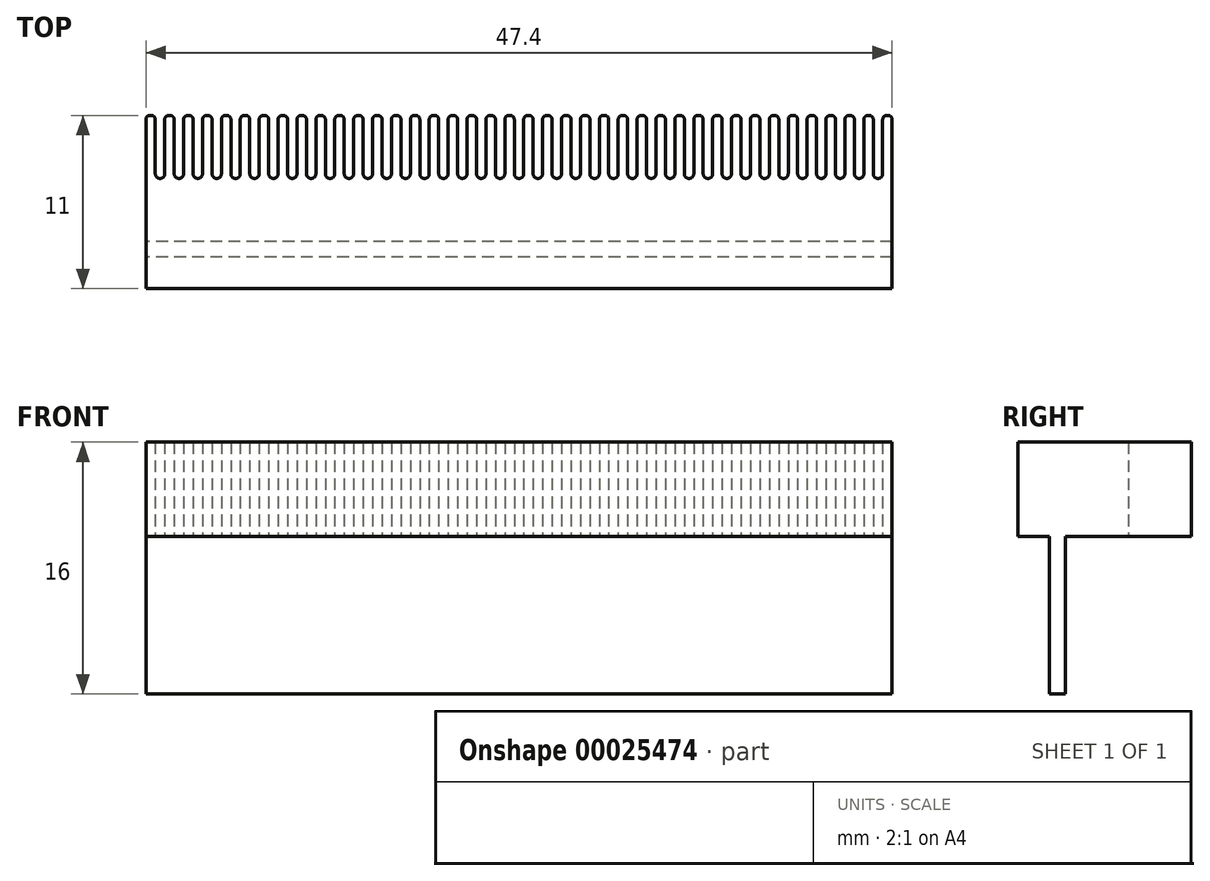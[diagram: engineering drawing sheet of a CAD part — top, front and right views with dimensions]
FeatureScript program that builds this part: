
annotation { "Feature Type Name" : "Feature", "Feature Type Description" : "" }
export const myFeature = defineFeature(function(context is Context, id is Id, definition is map)
    precondition{}
    {
        {
            var Q0;
            Q0=qCreatedBy(makeId("Top.planeOp"),FACE);
            var sketch = newSketch(context, id + "F0", { "sketchPlane" : qUnion([Q0])});
            skLineSegment(sketch, "E0", {"start": v(-0.6, 7) * mm, "end": v(-0.6, 7) * mm});
            skLineSegment(sketch, "E1", {"start": v(-0.3, 7.3) * mm, "end": v(-0.3, 10.75) * mm});
            skLineSegment(sketch, "E2", {"start": v(-0.05, 11) * mm, "end": v(0.05, 11) * mm});
            skLineSegment(sketch, "E3", {"start": v(0.3, 10.75) * mm, "end": v(0.3, 7.3) * mm});
            skLineSegment(sketch, "E4", {"start": v(0.6, 7) * mm, "end": v(0.6, 7) * mm});
            skLineSegment(sketch, "E5", {"start": v(0.6, 7) * mm, "end": v(0.6, 0) * mm});
            skLineSegment(sketch, "E6", {"start": v(0.6, 0) * mm, "end": v(-0.6, 0) * mm});
            skLineSegment(sketch, "E7", {"start": v(-0.6, 0) * mm, "end": v(-0.6, 7) * mm});
            skLineSegment(sketch, "E8.direction1", {"start": v(-7.3, 0) * mm, "end": v(-0.6, 0) * mm, "construction": true});
            skPoint(sketch, "E9.visualSharp", {"position": v(-0.3, 11) * mm});
            skArc(sketch, "E9.filletArc", {"start": v(-0.05, 11) * mm, "mid": v(-0.23, 10.93) * mm, "end": v(-0.3, 10.75) * mm});
            skPoint(sketch, "E10.visualSharp", {"position": v(0.3, 11) * mm});
            skArc(sketch, "E10.filletArc", {"start": v(0.3, 10.75) * mm, "mid": v(0.23, 10.93) * mm, "end": v(0.05, 11) * mm});
            skPoint(sketch, "E11.visualSharp", {"position": v(0.3, 7) * mm});
            skArc(sketch, "E11.filletArc", {"start": v(0.3, 7.3) * mm, "mid": v(0.39, 7.09) * mm, "end": v(0.6, 7) * mm});
            skPoint(sketch, "E12.visualSharp", {"position": v(-0.3, 7) * mm});
            skArc(sketch, "E12.filletArc", {"start": v(-0.6, 7) * mm, "mid": v(-0.39, 7.09) * mm, "end": v(-0.3, 7.3) * mm});
            skLineSegment(sketch, "E13.1.0.0", {"start": v(1.8, 0) * mm, "end": v(0.6, 0) * mm});
            skPoint(sketch, "E13.1.0.1", {"position": v(1.5, 7) * mm});
            skLineSegment(sketch, "E13.1.0.2", {"start": v(1.8, 7) * mm, "end": v(1.8, 0) * mm});
            skLineSegment(sketch, "E13.1.0.3", {"start": v(1.5, 10.75) * mm, "end": v(1.5, 7.3) * mm});
            skPoint(sketch, "E13.1.0.4", {"position": v(1.5, 11) * mm});
            skPoint(sketch, "E13.1.0.5", {"position": v(0.9, 7) * mm});
            skLineSegment(sketch, "E13.1.0.6", {"start": v(0.6, 0) * mm, "end": v(0.6, 7) * mm});
            skPoint(sketch, "E13.1.0.7", {"position": v(0.9, 11) * mm});
            skLineSegment(sketch, "E13.1.0.8", {"start": v(0.9, 7.3) * mm, "end": v(0.9, 10.75) * mm});
            skArc(sketch, "E13.1.0.9", {"start": v(1.5, 10.75) * mm, "mid": v(1.43, 10.93) * mm, "end": v(1.25, 11) * mm});
            skLineSegment(sketch, "E13.1.0.10", {"start": v(-6.1, 0) * mm, "end": v(0.6, 0) * mm, "construction": true});
            skArc(sketch, "E13.1.0.11", {"start": v(1.15, 11) * mm, "mid": v(0.97, 10.93) * mm, "end": v(0.9, 10.75) * mm});
            skArc(sketch, "E13.1.0.12", {"start": v(0.6, 7) * mm, "mid": v(0.81, 7.09) * mm, "end": v(0.9, 7.3) * mm});
            skArc(sketch, "E13.1.0.13", {"start": v(1.5, 7.3) * mm, "mid": v(1.59, 7.09) * mm, "end": v(1.8, 7) * mm});
            skLineSegment(sketch, "E13.1.0.14", {"start": v(1.15, 11) * mm, "end": v(1.25, 11) * mm});
            skLineSegment(sketch, "E13.2.0.0", {"start": v(3, 0) * mm, "end": v(1.8, 0) * mm});
            skPoint(sketch, "E13.2.0.1", {"position": v(2.7, 7) * mm});
            skLineSegment(sketch, "E13.2.0.2", {"start": v(3, 7) * mm, "end": v(3, 0) * mm});
            skLineSegment(sketch, "E13.2.0.3", {"start": v(2.7, 10.75) * mm, "end": v(2.7, 7.3) * mm});
            skPoint(sketch, "E13.2.0.4", {"position": v(2.7, 11) * mm});
            skPoint(sketch, "E13.2.0.5", {"position": v(2.1, 7) * mm});
            skLineSegment(sketch, "E13.2.0.6", {"start": v(1.8, 0) * mm, "end": v(1.8, 7) * mm});
            skPoint(sketch, "E13.2.0.7", {"position": v(2.1, 11) * mm});
            skLineSegment(sketch, "E13.2.0.8", {"start": v(2.1, 7.3) * mm, "end": v(2.1, 10.75) * mm});
            skArc(sketch, "E13.2.0.9", {"start": v(2.7, 10.75) * mm, "mid": v(2.63, 10.93) * mm, "end": v(2.45, 11) * mm});
            skLineSegment(sketch, "E13.2.0.10", {"start": v(-4.9, 0) * mm, "end": v(1.8, 0) * mm, "construction": true});
            skArc(sketch, "E13.2.0.11", {"start": v(2.35, 11) * mm, "mid": v(2.17, 10.93) * mm, "end": v(2.1, 10.75) * mm});
            skArc(sketch, "E13.2.0.12", {"start": v(1.8, 7) * mm, "mid": v(2.01, 7.09) * mm, "end": v(2.1, 7.3) * mm});
            skArc(sketch, "E13.2.0.13", {"start": v(2.7, 7.3) * mm, "mid": v(2.79, 7.09) * mm, "end": v(3, 7) * mm});
            skLineSegment(sketch, "E13.2.0.14", {"start": v(2.35, 11) * mm, "end": v(2.45, 11) * mm});
            skLineSegment(sketch, "E13.3.0.0", {"start": v(4.2, 0) * mm, "end": v(3, 0) * mm});
            skPoint(sketch, "E13.3.0.1", {"position": v(3.9, 7) * mm});
            skLineSegment(sketch, "E13.3.0.2", {"start": v(4.2, 7) * mm, "end": v(4.2, 0) * mm});
            skLineSegment(sketch, "E13.3.0.3", {"start": v(3.9, 10.75) * mm, "end": v(3.9, 7.3) * mm});
            skPoint(sketch, "E13.3.0.4", {"position": v(3.9, 11) * mm});
            skPoint(sketch, "E13.3.0.5", {"position": v(3.3, 7) * mm});
            skLineSegment(sketch, "E13.3.0.6", {"start": v(3, 0) * mm, "end": v(3, 7) * mm});
            skPoint(sketch, "E13.3.0.7", {"position": v(3.3, 11) * mm});
            skLineSegment(sketch, "E13.3.0.8", {"start": v(3.3, 7.3) * mm, "end": v(3.3, 10.75) * mm});
            skArc(sketch, "E13.3.0.9", {"start": v(3.9, 10.75) * mm, "mid": v(3.83, 10.93) * mm, "end": v(3.65, 11) * mm});
            skLineSegment(sketch, "E13.3.0.10", {"start": v(-3.7, 0) * mm, "end": v(3, 0) * mm, "construction": true});
            skArc(sketch, "E13.3.0.11", {"start": v(3.55, 11) * mm, "mid": v(3.37, 10.93) * mm, "end": v(3.3, 10.75) * mm});
            skArc(sketch, "E13.3.0.12", {"start": v(3, 7) * mm, "mid": v(3.21, 7.09) * mm, "end": v(3.3, 7.3) * mm});
            skArc(sketch, "E13.3.0.13", {"start": v(3.9, 7.3) * mm, "mid": v(3.99, 7.09) * mm, "end": v(4.2, 7) * mm});
            skLineSegment(sketch, "E13.3.0.14", {"start": v(3.55, 11) * mm, "end": v(3.65, 11) * mm});
            skLineSegment(sketch, "E13.4.0.0", {"start": v(5.4, 0) * mm, "end": v(4.2, 0) * mm});
            skPoint(sketch, "E13.4.0.1", {"position": v(5.1, 7) * mm});
            skLineSegment(sketch, "E13.4.0.2", {"start": v(5.4, 7) * mm, "end": v(5.4, 0) * mm});
            skLineSegment(sketch, "E13.4.0.3", {"start": v(5.1, 10.75) * mm, "end": v(5.1, 7.3) * mm});
            skPoint(sketch, "E13.4.0.4", {"position": v(5.1, 11) * mm});
            skPoint(sketch, "E13.4.0.5", {"position": v(4.5, 7) * mm});
            skLineSegment(sketch, "E13.4.0.6", {"start": v(4.2, 0) * mm, "end": v(4.2, 7) * mm});
            skPoint(sketch, "E13.4.0.7", {"position": v(4.5, 11) * mm});
            skLineSegment(sketch, "E13.4.0.8", {"start": v(4.5, 7.3) * mm, "end": v(4.5, 10.75) * mm});
            skArc(sketch, "E13.4.0.9", {"start": v(5.1, 10.75) * mm, "mid": v(5.03, 10.93) * mm, "end": v(4.85, 11) * mm});
            skLineSegment(sketch, "E13.4.0.10", {"start": v(-2.5, 0) * mm, "end": v(4.2, 0) * mm, "construction": true});
            skArc(sketch, "E13.4.0.11", {"start": v(4.75, 11) * mm, "mid": v(4.57, 10.93) * mm, "end": v(4.5, 10.75) * mm});
            skArc(sketch, "E13.4.0.12", {"start": v(4.2, 7) * mm, "mid": v(4.41, 7.09) * mm, "end": v(4.5, 7.3) * mm});
            skArc(sketch, "E13.4.0.13", {"start": v(5.1, 7.3) * mm, "mid": v(5.19, 7.09) * mm, "end": v(5.4, 7) * mm});
            skLineSegment(sketch, "E13.4.0.14", {"start": v(4.75, 11) * mm, "end": v(4.85, 11) * mm});
            skLineSegment(sketch, "E13.5.0.0", {"start": v(6.6, 0) * mm, "end": v(5.4, 0) * mm});
            skPoint(sketch, "E13.5.0.1", {"position": v(6.3, 7) * mm});
            skLineSegment(sketch, "E13.5.0.2", {"start": v(6.6, 7) * mm, "end": v(6.6, 0) * mm});
            skLineSegment(sketch, "E13.5.0.3", {"start": v(6.3, 10.75) * mm, "end": v(6.3, 7.3) * mm});
            skPoint(sketch, "E13.5.0.4", {"position": v(6.3, 11) * mm});
            skPoint(sketch, "E13.5.0.5", {"position": v(5.7, 7) * mm});
            skLineSegment(sketch, "E13.5.0.6", {"start": v(5.4, 0) * mm, "end": v(5.4, 7) * mm});
            skPoint(sketch, "E13.5.0.7", {"position": v(5.7, 11) * mm});
            skLineSegment(sketch, "E13.5.0.8", {"start": v(5.7, 7.3) * mm, "end": v(5.7, 10.75) * mm});
            skArc(sketch, "E13.5.0.9", {"start": v(6.3, 10.75) * mm, "mid": v(6.23, 10.93) * mm, "end": v(6.05, 11) * mm});
            skLineSegment(sketch, "E13.5.0.10", {"start": v(-1.3, 0) * mm, "end": v(5.4, 0) * mm, "construction": true});
            skArc(sketch, "E13.5.0.11", {"start": v(5.95, 11) * mm, "mid": v(5.77, 10.93) * mm, "end": v(5.7, 10.75) * mm});
            skArc(sketch, "E13.5.0.12", {"start": v(5.4, 7) * mm, "mid": v(5.61, 7.09) * mm, "end": v(5.7, 7.3) * mm});
            skArc(sketch, "E13.5.0.13", {"start": v(6.3, 7.3) * mm, "mid": v(6.39, 7.09) * mm, "end": v(6.6, 7) * mm});
            skLineSegment(sketch, "E13.5.0.14", {"start": v(5.95, 11) * mm, "end": v(6.05, 11) * mm});
            skLineSegment(sketch, "E13.6.0.0", {"start": v(7.8, 0) * mm, "end": v(6.6, 0) * mm});
            skPoint(sketch, "E13.6.0.1", {"position": v(7.5, 7) * mm});
            skLineSegment(sketch, "E13.6.0.2", {"start": v(7.8, 7) * mm, "end": v(7.8, 0) * mm});
            skLineSegment(sketch, "E13.6.0.3", {"start": v(7.5, 10.75) * mm, "end": v(7.5, 7.3) * mm});
            skPoint(sketch, "E13.6.0.4", {"position": v(7.5, 11) * mm});
            skPoint(sketch, "E13.6.0.5", {"position": v(6.9, 7) * mm});
            skLineSegment(sketch, "E13.6.0.6", {"start": v(6.6, 0) * mm, "end": v(6.6, 7) * mm});
            skPoint(sketch, "E13.6.0.7", {"position": v(6.9, 11) * mm});
            skLineSegment(sketch, "E13.6.0.8", {"start": v(6.9, 7.3) * mm, "end": v(6.9, 10.75) * mm});
            skArc(sketch, "E13.6.0.9", {"start": v(7.5, 10.75) * mm, "mid": v(7.43, 10.93) * mm, "end": v(7.25, 11) * mm});
            skLineSegment(sketch, "E13.6.0.10", {"start": v(-0.1, 0) * mm, "end": v(6.6, 0) * mm, "construction": true});
            skArc(sketch, "E13.6.0.11", {"start": v(7.15, 11) * mm, "mid": v(6.97, 10.93) * mm, "end": v(6.9, 10.75) * mm});
            skArc(sketch, "E13.6.0.12", {"start": v(6.6, 7) * mm, "mid": v(6.81, 7.09) * mm, "end": v(6.9, 7.3) * mm});
            skArc(sketch, "E13.6.0.13", {"start": v(7.5, 7.3) * mm, "mid": v(7.59, 7.09) * mm, "end": v(7.8, 7) * mm});
            skLineSegment(sketch, "E13.6.0.14", {"start": v(7.15, 11) * mm, "end": v(7.25, 11) * mm});
            skLineSegment(sketch, "E13.7.0.0", {"start": v(9, 0) * mm, "end": v(7.8, 0) * mm});
            skPoint(sketch, "E13.7.0.1", {"position": v(8.7, 7) * mm});
            skLineSegment(sketch, "E13.7.0.2", {"start": v(9, 7) * mm, "end": v(9, 0) * mm});
            skLineSegment(sketch, "E13.7.0.3", {"start": v(8.7, 10.75) * mm, "end": v(8.7, 7.3) * mm});
            skPoint(sketch, "E13.7.0.4", {"position": v(8.7, 11) * mm});
            skPoint(sketch, "E13.7.0.5", {"position": v(8.1, 7) * mm});
            skLineSegment(sketch, "E13.7.0.6", {"start": v(7.8, 0) * mm, "end": v(7.8, 7) * mm});
            skPoint(sketch, "E13.7.0.7", {"position": v(8.1, 11) * mm});
            skLineSegment(sketch, "E13.7.0.8", {"start": v(8.1, 7.3) * mm, "end": v(8.1, 10.75) * mm});
            skArc(sketch, "E13.7.0.9", {"start": v(8.7, 10.75) * mm, "mid": v(8.63, 10.93) * mm, "end": v(8.45, 11) * mm});
            skLineSegment(sketch, "E13.7.0.10", {"start": v(1.1, 0) * mm, "end": v(7.8, 0) * mm, "construction": true});
            skArc(sketch, "E13.7.0.11", {"start": v(8.35, 11) * mm, "mid": v(8.17, 10.93) * mm, "end": v(8.1, 10.75) * mm});
            skArc(sketch, "E13.7.0.12", {"start": v(7.8, 7) * mm, "mid": v(8.01, 7.09) * mm, "end": v(8.1, 7.3) * mm});
            skArc(sketch, "E13.7.0.13", {"start": v(8.7, 7.3) * mm, "mid": v(8.79, 7.09) * mm, "end": v(9, 7) * mm});
            skLineSegment(sketch, "E13.7.0.14", {"start": v(8.35, 11) * mm, "end": v(8.45, 11) * mm});
            skLineSegment(sketch, "E13.8.0.0", {"start": v(10.2, 0) * mm, "end": v(9, 0) * mm});
            skPoint(sketch, "E13.8.0.1", {"position": v(9.9, 7) * mm});
            skLineSegment(sketch, "E13.8.0.2", {"start": v(10.2, 7) * mm, "end": v(10.2, 0) * mm});
            skLineSegment(sketch, "E13.8.0.3", {"start": v(9.9, 10.75) * mm, "end": v(9.9, 7.3) * mm});
            skPoint(sketch, "E13.8.0.4", {"position": v(9.9, 11) * mm});
            skPoint(sketch, "E13.8.0.5", {"position": v(9.3, 7) * mm});
            skLineSegment(sketch, "E13.8.0.6", {"start": v(9, 0) * mm, "end": v(9, 7) * mm});
            skPoint(sketch, "E13.8.0.7", {"position": v(9.3, 11) * mm});
            skLineSegment(sketch, "E13.8.0.8", {"start": v(9.3, 7.3) * mm, "end": v(9.3, 10.75) * mm});
            skArc(sketch, "E13.8.0.9", {"start": v(9.9, 10.75) * mm, "mid": v(9.83, 10.93) * mm, "end": v(9.65, 11) * mm});
            skLineSegment(sketch, "E13.8.0.10", {"start": v(2.3, 0) * mm, "end": v(9, 0) * mm, "construction": true});
            skArc(sketch, "E13.8.0.11", {"start": v(9.55, 11) * mm, "mid": v(9.37, 10.93) * mm, "end": v(9.3, 10.75) * mm});
            skArc(sketch, "E13.8.0.12", {"start": v(9, 7) * mm, "mid": v(9.21, 7.09) * mm, "end": v(9.3, 7.3) * mm});
            skArc(sketch, "E13.8.0.13", {"start": v(9.9, 7.3) * mm, "mid": v(9.99, 7.09) * mm, "end": v(10.2, 7) * mm});
            skLineSegment(sketch, "E13.8.0.14", {"start": v(9.55, 11) * mm, "end": v(9.65, 11) * mm});
            skLineSegment(sketch, "E13.9.0.0", {"start": v(11.4, 0) * mm, "end": v(10.2, 0) * mm});
            skPoint(sketch, "E13.9.0.1", {"position": v(11.1, 7) * mm});
            skLineSegment(sketch, "E13.9.0.2", {"start": v(11.4, 7) * mm, "end": v(11.4, 0) * mm});
            skLineSegment(sketch, "E13.9.0.3", {"start": v(11.1, 10.75) * mm, "end": v(11.1, 7.3) * mm});
            skPoint(sketch, "E13.9.0.4", {"position": v(11.1, 11) * mm});
            skPoint(sketch, "E13.9.0.5", {"position": v(10.5, 7) * mm});
            skLineSegment(sketch, "E13.9.0.6", {"start": v(10.2, 0) * mm, "end": v(10.2, 7) * mm});
            skPoint(sketch, "E13.9.0.7", {"position": v(10.5, 11) * mm});
            skLineSegment(sketch, "E13.9.0.8", {"start": v(10.5, 7.3) * mm, "end": v(10.5, 10.75) * mm});
            skArc(sketch, "E13.9.0.9", {"start": v(11.1, 10.75) * mm, "mid": v(11.03, 10.93) * mm, "end": v(10.85, 11) * mm});
            skLineSegment(sketch, "E13.9.0.10", {"start": v(3.5, 0) * mm, "end": v(10.2, 0) * mm, "construction": true});
            skArc(sketch, "E13.9.0.11", {"start": v(10.75, 11) * mm, "mid": v(10.57, 10.93) * mm, "end": v(10.5, 10.75) * mm});
            skArc(sketch, "E13.9.0.12", {"start": v(10.2, 7) * mm, "mid": v(10.41, 7.09) * mm, "end": v(10.5, 7.3) * mm});
            skArc(sketch, "E13.9.0.13", {"start": v(11.1, 7.3) * mm, "mid": v(11.19, 7.09) * mm, "end": v(11.4, 7) * mm});
            skLineSegment(sketch, "E13.9.0.14", {"start": v(10.75, 11) * mm, "end": v(10.85, 11) * mm});
            skLineSegment(sketch, "E13.10.0.0", {"start": v(12.6, 0) * mm, "end": v(11.4, 0) * mm});
            skPoint(sketch, "E13.10.0.1", {"position": v(12.3, 7) * mm});
            skLineSegment(sketch, "E13.10.0.2", {"start": v(12.6, 7) * mm, "end": v(12.6, 0) * mm});
            skLineSegment(sketch, "E13.10.0.3", {"start": v(12.3, 10.75) * mm, "end": v(12.3, 7.3) * mm});
            skPoint(sketch, "E13.10.0.4", {"position": v(12.3, 11) * mm});
            skPoint(sketch, "E13.10.0.5", {"position": v(11.7, 7) * mm});
            skLineSegment(sketch, "E13.10.0.6", {"start": v(11.4, 0) * mm, "end": v(11.4, 7) * mm});
            skPoint(sketch, "E13.10.0.7", {"position": v(11.7, 11) * mm});
            skLineSegment(sketch, "E13.10.0.8", {"start": v(11.7, 7.3) * mm, "end": v(11.7, 10.75) * mm});
            skArc(sketch, "E13.10.0.9", {"start": v(12.3, 10.75) * mm, "mid": v(12.23, 10.93) * mm, "end": v(12.05, 11) * mm});
            skLineSegment(sketch, "E13.10.0.10", {"start": v(4.7, 0) * mm, "end": v(11.4, 0) * mm, "construction": true});
            skArc(sketch, "E13.10.0.11", {"start": v(11.95, 11) * mm, "mid": v(11.77, 10.93) * mm, "end": v(11.7, 10.75) * mm});
            skArc(sketch, "E13.10.0.12", {"start": v(11.4, 7) * mm, "mid": v(11.61, 7.09) * mm, "end": v(11.7, 7.3) * mm});
            skArc(sketch, "E13.10.0.13", {"start": v(12.3, 7.3) * mm, "mid": v(12.39, 7.09) * mm, "end": v(12.6, 7) * mm});
            skLineSegment(sketch, "E13.10.0.14", {"start": v(11.95, 11) * mm, "end": v(12.05, 11) * mm});
            skLineSegment(sketch, "E13.11.0.0", {"start": v(13.8, 0) * mm, "end": v(12.6, 0) * mm});
            skPoint(sketch, "E13.11.0.1", {"position": v(13.5, 7) * mm});
            skLineSegment(sketch, "E13.11.0.2", {"start": v(13.8, 7) * mm, "end": v(13.8, 0) * mm});
            skLineSegment(sketch, "E13.11.0.3", {"start": v(13.5, 10.75) * mm, "end": v(13.5, 7.3) * mm});
            skPoint(sketch, "E13.11.0.4", {"position": v(13.5, 11) * mm});
            skPoint(sketch, "E13.11.0.5", {"position": v(12.9, 7) * mm});
            skLineSegment(sketch, "E13.11.0.6", {"start": v(12.6, 0) * mm, "end": v(12.6, 7) * mm});
            skPoint(sketch, "E13.11.0.7", {"position": v(12.9, 11) * mm});
            skLineSegment(sketch, "E13.11.0.8", {"start": v(12.9, 7.3) * mm, "end": v(12.9, 10.75) * mm});
            skArc(sketch, "E13.11.0.9", {"start": v(13.5, 10.75) * mm, "mid": v(13.43, 10.93) * mm, "end": v(13.25, 11) * mm});
            skLineSegment(sketch, "E13.11.0.10", {"start": v(5.9, 0) * mm, "end": v(12.6, 0) * mm, "construction": true});
            skArc(sketch, "E13.11.0.11", {"start": v(13.15, 11) * mm, "mid": v(12.97, 10.93) * mm, "end": v(12.9, 10.75) * mm});
            skArc(sketch, "E13.11.0.12", {"start": v(12.6, 7) * mm, "mid": v(12.81, 7.09) * mm, "end": v(12.9, 7.3) * mm});
            skArc(sketch, "E13.11.0.13", {"start": v(13.5, 7.3) * mm, "mid": v(13.59, 7.09) * mm, "end": v(13.8, 7) * mm});
            skLineSegment(sketch, "E13.11.0.14", {"start": v(13.15, 11) * mm, "end": v(13.25, 11) * mm});
            skLineSegment(sketch, "E13.12.0.0", {"start": v(15, 0) * mm, "end": v(13.8, 0) * mm});
            skPoint(sketch, "E13.12.0.1", {"position": v(14.7, 7) * mm});
            skLineSegment(sketch, "E13.12.0.2", {"start": v(15, 7) * mm, "end": v(15, 0) * mm});
            skLineSegment(sketch, "E13.12.0.3", {"start": v(14.7, 10.75) * mm, "end": v(14.7, 7.3) * mm});
            skPoint(sketch, "E13.12.0.4", {"position": v(14.7, 11) * mm});
            skPoint(sketch, "E13.12.0.5", {"position": v(14.1, 7) * mm});
            skLineSegment(sketch, "E13.12.0.6", {"start": v(13.8, 0) * mm, "end": v(13.8, 7) * mm});
            skPoint(sketch, "E13.12.0.7", {"position": v(14.1, 11) * mm});
            skLineSegment(sketch, "E13.12.0.8", {"start": v(14.1, 7.3) * mm, "end": v(14.1, 10.75) * mm});
            skArc(sketch, "E13.12.0.9", {"start": v(14.7, 10.75) * mm, "mid": v(14.63, 10.93) * mm, "end": v(14.45, 11) * mm});
            skLineSegment(sketch, "E13.12.0.10", {"start": v(7.1, 0) * mm, "end": v(13.8, 0) * mm, "construction": true});
            skArc(sketch, "E13.12.0.11", {"start": v(14.35, 11) * mm, "mid": v(14.17, 10.93) * mm, "end": v(14.1, 10.75) * mm});
            skArc(sketch, "E13.12.0.12", {"start": v(13.8, 7) * mm, "mid": v(14.01, 7.09) * mm, "end": v(14.1, 7.3) * mm});
            skArc(sketch, "E13.12.0.13", {"start": v(14.7, 7.3) * mm, "mid": v(14.79, 7.09) * mm, "end": v(15, 7) * mm});
            skLineSegment(sketch, "E13.12.0.14", {"start": v(14.35, 11) * mm, "end": v(14.45, 11) * mm});
            skLineSegment(sketch, "E13.13.0.0", {"start": v(16.2, 0) * mm, "end": v(15, 0) * mm});
            skPoint(sketch, "E13.13.0.1", {"position": v(15.9, 7) * mm});
            skLineSegment(sketch, "E13.13.0.2", {"start": v(16.2, 7) * mm, "end": v(16.2, 0) * mm});
            skLineSegment(sketch, "E13.13.0.3", {"start": v(15.9, 10.75) * mm, "end": v(15.9, 7.3) * mm});
            skPoint(sketch, "E13.13.0.4", {"position": v(15.9, 11) * mm});
            skPoint(sketch, "E13.13.0.5", {"position": v(15.3, 7) * mm});
            skLineSegment(sketch, "E13.13.0.6", {"start": v(15, 0) * mm, "end": v(15, 7) * mm});
            skPoint(sketch, "E13.13.0.7", {"position": v(15.3, 11) * mm});
            skLineSegment(sketch, "E13.13.0.8", {"start": v(15.3, 7.3) * mm, "end": v(15.3, 10.75) * mm});
            skArc(sketch, "E13.13.0.9", {"start": v(15.9, 10.75) * mm, "mid": v(15.83, 10.93) * mm, "end": v(15.65, 11) * mm});
            skLineSegment(sketch, "E13.13.0.10", {"start": v(8.3, 0) * mm, "end": v(15, 0) * mm, "construction": true});
            skArc(sketch, "E13.13.0.11", {"start": v(15.55, 11) * mm, "mid": v(15.37, 10.93) * mm, "end": v(15.3, 10.75) * mm});
            skArc(sketch, "E13.13.0.12", {"start": v(15, 7) * mm, "mid": v(15.21, 7.09) * mm, "end": v(15.3, 7.3) * mm});
            skArc(sketch, "E13.13.0.13", {"start": v(15.9, 7.3) * mm, "mid": v(15.99, 7.09) * mm, "end": v(16.2, 7) * mm});
            skLineSegment(sketch, "E13.13.0.14", {"start": v(15.55, 11) * mm, "end": v(15.65, 11) * mm});
            skLineSegment(sketch, "E13.14.0.0", {"start": v(17.4, 0) * mm, "end": v(16.2, 0) * mm});
            skPoint(sketch, "E13.14.0.1", {"position": v(17.1, 7) * mm});
            skLineSegment(sketch, "E13.14.0.2", {"start": v(17.4, 7) * mm, "end": v(17.4, 0) * mm});
            skLineSegment(sketch, "E13.14.0.3", {"start": v(17.1, 10.75) * mm, "end": v(17.1, 7.3) * mm});
            skPoint(sketch, "E13.14.0.4", {"position": v(17.1, 11) * mm});
            skPoint(sketch, "E13.14.0.5", {"position": v(16.5, 7) * mm});
            skLineSegment(sketch, "E13.14.0.6", {"start": v(16.2, 0) * mm, "end": v(16.2, 7) * mm});
            skPoint(sketch, "E13.14.0.7", {"position": v(16.5, 11) * mm});
            skLineSegment(sketch, "E13.14.0.8", {"start": v(16.5, 7.3) * mm, "end": v(16.5, 10.75) * mm});
            skArc(sketch, "E13.14.0.9", {"start": v(17.1, 10.75) * mm, "mid": v(17.03, 10.93) * mm, "end": v(16.85, 11) * mm});
            skLineSegment(sketch, "E13.14.0.10", {"start": v(9.5, 0) * mm, "end": v(16.2, 0) * mm, "construction": true});
            skArc(sketch, "E13.14.0.11", {"start": v(16.75, 11) * mm, "mid": v(16.57, 10.93) * mm, "end": v(16.5, 10.75) * mm});
            skArc(sketch, "E13.14.0.12", {"start": v(16.2, 7) * mm, "mid": v(16.41, 7.09) * mm, "end": v(16.5, 7.3) * mm});
            skArc(sketch, "E13.14.0.13", {"start": v(17.1, 7.3) * mm, "mid": v(17.19, 7.09) * mm, "end": v(17.4, 7) * mm});
            skLineSegment(sketch, "E13.14.0.14", {"start": v(16.75, 11) * mm, "end": v(16.85, 11) * mm});
            skLineSegment(sketch, "E13.15.0.0", {"start": v(18.6, 0) * mm, "end": v(17.4, 0) * mm});
            skPoint(sketch, "E13.15.0.1", {"position": v(18.3, 7) * mm});
            skLineSegment(sketch, "E13.15.0.2", {"start": v(18.6, 7) * mm, "end": v(18.6, 0) * mm});
            skLineSegment(sketch, "E13.15.0.3", {"start": v(18.3, 10.75) * mm, "end": v(18.3, 7.3) * mm});
            skPoint(sketch, "E13.15.0.4", {"position": v(18.3, 11) * mm});
            skPoint(sketch, "E13.15.0.5", {"position": v(17.7, 7) * mm});
            skLineSegment(sketch, "E13.15.0.6", {"start": v(17.4, 0) * mm, "end": v(17.4, 7) * mm});
            skPoint(sketch, "E13.15.0.7", {"position": v(17.7, 11) * mm});
            skLineSegment(sketch, "E13.15.0.8", {"start": v(17.7, 7.3) * mm, "end": v(17.7, 10.75) * mm});
            skArc(sketch, "E13.15.0.9", {"start": v(18.3, 10.75) * mm, "mid": v(18.23, 10.93) * mm, "end": v(18.05, 11) * mm});
            skLineSegment(sketch, "E13.15.0.10", {"start": v(10.7, 0) * mm, "end": v(17.4, 0) * mm, "construction": true});
            skArc(sketch, "E13.15.0.11", {"start": v(17.95, 11) * mm, "mid": v(17.77, 10.93) * mm, "end": v(17.7, 10.75) * mm});
            skArc(sketch, "E13.15.0.12", {"start": v(17.4, 7) * mm, "mid": v(17.61, 7.09) * mm, "end": v(17.7, 7.3) * mm});
            skArc(sketch, "E13.15.0.13", {"start": v(18.3, 7.3) * mm, "mid": v(18.39, 7.09) * mm, "end": v(18.6, 7) * mm});
            skLineSegment(sketch, "E13.15.0.14", {"start": v(17.95, 11) * mm, "end": v(18.05, 11) * mm});
            skLineSegment(sketch, "E13.16.0.0", {"start": v(19.8, 0) * mm, "end": v(18.6, 0) * mm});
            skPoint(sketch, "E13.16.0.1", {"position": v(19.5, 7) * mm});
            skLineSegment(sketch, "E13.16.0.2", {"start": v(19.8, 7) * mm, "end": v(19.8, 0) * mm});
            skLineSegment(sketch, "E13.16.0.3", {"start": v(19.5, 10.75) * mm, "end": v(19.5, 7.3) * mm});
            skPoint(sketch, "E13.16.0.4", {"position": v(19.5, 11) * mm});
            skPoint(sketch, "E13.16.0.5", {"position": v(18.9, 7) * mm});
            skLineSegment(sketch, "E13.16.0.6", {"start": v(18.6, 0) * mm, "end": v(18.6, 7) * mm});
            skPoint(sketch, "E13.16.0.7", {"position": v(18.9, 11) * mm});
            skLineSegment(sketch, "E13.16.0.8", {"start": v(18.9, 7.3) * mm, "end": v(18.9, 10.75) * mm});
            skArc(sketch, "E13.16.0.9", {"start": v(19.5, 10.75) * mm, "mid": v(19.43, 10.93) * mm, "end": v(19.25, 11) * mm});
            skLineSegment(sketch, "E13.16.0.10", {"start": v(11.9, 0) * mm, "end": v(18.6, 0) * mm, "construction": true});
            skArc(sketch, "E13.16.0.11", {"start": v(19.15, 11) * mm, "mid": v(18.97, 10.93) * mm, "end": v(18.9, 10.75) * mm});
            skArc(sketch, "E13.16.0.12", {"start": v(18.6, 7) * mm, "mid": v(18.81, 7.09) * mm, "end": v(18.9, 7.3) * mm});
            skArc(sketch, "E13.16.0.13", {"start": v(19.5, 7.3) * mm, "mid": v(19.59, 7.09) * mm, "end": v(19.8, 7) * mm});
            skLineSegment(sketch, "E13.16.0.14", {"start": v(19.15, 11) * mm, "end": v(19.25, 11) * mm});
            skLineSegment(sketch, "E13.17.0.0", {"start": v(21, 0) * mm, "end": v(19.8, 0) * mm});
            skPoint(sketch, "E13.17.0.1", {"position": v(20.7, 7) * mm});
            skLineSegment(sketch, "E13.17.0.2", {"start": v(21, 7) * mm, "end": v(21, 0) * mm});
            skLineSegment(sketch, "E13.17.0.3", {"start": v(20.7, 10.75) * mm, "end": v(20.7, 7.3) * mm});
            skPoint(sketch, "E13.17.0.4", {"position": v(20.7, 11) * mm});
            skPoint(sketch, "E13.17.0.5", {"position": v(20.1, 7) * mm});
            skLineSegment(sketch, "E13.17.0.6", {"start": v(19.8, 0) * mm, "end": v(19.8, 7) * mm});
            skPoint(sketch, "E13.17.0.7", {"position": v(20.1, 11) * mm});
            skLineSegment(sketch, "E13.17.0.8", {"start": v(20.1, 7.3) * mm, "end": v(20.1, 10.75) * mm});
            skArc(sketch, "E13.17.0.9", {"start": v(20.7, 10.75) * mm, "mid": v(20.63, 10.93) * mm, "end": v(20.45, 11) * mm});
            skLineSegment(sketch, "E13.17.0.10", {"start": v(13.1, 0) * mm, "end": v(19.8, 0) * mm, "construction": true});
            skArc(sketch, "E13.17.0.11", {"start": v(20.35, 11) * mm, "mid": v(20.17, 10.93) * mm, "end": v(20.1, 10.75) * mm});
            skArc(sketch, "E13.17.0.12", {"start": v(19.8, 7) * mm, "mid": v(20.01, 7.09) * mm, "end": v(20.1, 7.3) * mm});
            skArc(sketch, "E13.17.0.13", {"start": v(20.7, 7.3) * mm, "mid": v(20.79, 7.09) * mm, "end": v(21, 7) * mm});
            skLineSegment(sketch, "E13.17.0.14", {"start": v(20.35, 11) * mm, "end": v(20.45, 11) * mm});
            skLineSegment(sketch, "E13.18.0.0", {"start": v(22.2, 0) * mm, "end": v(21, 0) * mm});
            skPoint(sketch, "E13.18.0.1", {"position": v(21.9, 7) * mm});
            skLineSegment(sketch, "E13.18.0.2", {"start": v(22.2, 7) * mm, "end": v(22.2, 0) * mm});
            skLineSegment(sketch, "E13.18.0.3", {"start": v(21.9, 10.75) * mm, "end": v(21.9, 7.3) * mm});
            skPoint(sketch, "E13.18.0.4", {"position": v(21.9, 11) * mm});
            skPoint(sketch, "E13.18.0.5", {"position": v(21.3, 7) * mm});
            skLineSegment(sketch, "E13.18.0.6", {"start": v(21, 0) * mm, "end": v(21, 7) * mm});
            skPoint(sketch, "E13.18.0.7", {"position": v(21.3, 11) * mm});
            skLineSegment(sketch, "E13.18.0.8", {"start": v(21.3, 7.3) * mm, "end": v(21.3, 10.75) * mm});
            skArc(sketch, "E13.18.0.9", {"start": v(21.9, 10.75) * mm, "mid": v(21.83, 10.93) * mm, "end": v(21.65, 11) * mm});
            skLineSegment(sketch, "E13.18.0.10", {"start": v(14.3, 0) * mm, "end": v(21, 0) * mm, "construction": true});
            skArc(sketch, "E13.18.0.11", {"start": v(21.55, 11) * mm, "mid": v(21.37, 10.93) * mm, "end": v(21.3, 10.75) * mm});
            skArc(sketch, "E13.18.0.12", {"start": v(21, 7) * mm, "mid": v(21.21, 7.09) * mm, "end": v(21.3, 7.3) * mm});
            skArc(sketch, "E13.18.0.13", {"start": v(21.9, 7.3) * mm, "mid": v(21.99, 7.09) * mm, "end": v(22.2, 7) * mm});
            skLineSegment(sketch, "E13.18.0.14", {"start": v(21.55, 11) * mm, "end": v(21.65, 11) * mm});
            skLineSegment(sketch, "E13.19.0.0", {"start": v(23.4, 0) * mm, "end": v(22.2, 0) * mm});
            skPoint(sketch, "E13.19.0.1", {"position": v(23.1, 7) * mm});
            skLineSegment(sketch, "E13.19.0.2", {"start": v(23.4, 7) * mm, "end": v(23.4, 0) * mm});
            skLineSegment(sketch, "E13.19.0.3", {"start": v(23.1, 10.75) * mm, "end": v(23.1, 7.3) * mm});
            skPoint(sketch, "E13.19.0.4", {"position": v(23.1, 11) * mm});
            skPoint(sketch, "E13.19.0.5", {"position": v(22.5, 7) * mm});
            skLineSegment(sketch, "E13.19.0.6", {"start": v(22.2, 0) * mm, "end": v(22.2, 7) * mm});
            skPoint(sketch, "E13.19.0.7", {"position": v(22.5, 11) * mm});
            skLineSegment(sketch, "E13.19.0.8", {"start": v(22.5, 7.3) * mm, "end": v(22.5, 10.75) * mm});
            skArc(sketch, "E13.19.0.9", {"start": v(23.1, 10.75) * mm, "mid": v(23.03, 10.93) * mm, "end": v(22.85, 11) * mm});
            skLineSegment(sketch, "E13.19.0.10", {"start": v(15.5, 0) * mm, "end": v(22.2, 0) * mm, "construction": true});
            skArc(sketch, "E13.19.0.11", {"start": v(22.75, 11) * mm, "mid": v(22.57, 10.93) * mm, "end": v(22.5, 10.75) * mm});
            skArc(sketch, "E13.19.0.12", {"start": v(22.2, 7) * mm, "mid": v(22.41, 7.09) * mm, "end": v(22.5, 7.3) * mm});
            skArc(sketch, "E13.19.0.13", {"start": v(23.1, 7.3) * mm, "mid": v(23.19, 7.09) * mm, "end": v(23.4, 7) * mm});
            skLineSegment(sketch, "E13.19.0.14", {"start": v(22.75, 11) * mm, "end": v(22.85, 11) * mm});
            skLineSegment(sketch, "E13.20.0.0", {"start": v(24.6, 0) * mm, "end": v(23.4, 0) * mm});
            skPoint(sketch, "E13.20.0.1", {"position": v(24.3, 7) * mm});
            skLineSegment(sketch, "E13.20.0.2", {"start": v(24.6, 7) * mm, "end": v(24.6, 0) * mm});
            skLineSegment(sketch, "E13.20.0.3", {"start": v(24.3, 10.75) * mm, "end": v(24.3, 7.3) * mm});
            skPoint(sketch, "E13.20.0.4", {"position": v(24.3, 11) * mm});
            skPoint(sketch, "E13.20.0.5", {"position": v(23.7, 7) * mm});
            skLineSegment(sketch, "E13.20.0.6", {"start": v(23.4, 0) * mm, "end": v(23.4, 7) * mm});
            skPoint(sketch, "E13.20.0.7", {"position": v(23.7, 11) * mm});
            skLineSegment(sketch, "E13.20.0.8", {"start": v(23.7, 7.3) * mm, "end": v(23.7, 10.75) * mm});
            skArc(sketch, "E13.20.0.9", {"start": v(24.3, 10.75) * mm, "mid": v(24.23, 10.93) * mm, "end": v(24.05, 11) * mm});
            skLineSegment(sketch, "E13.20.0.10", {"start": v(16.7, 0) * mm, "end": v(23.4, 0) * mm, "construction": true});
            skArc(sketch, "E13.20.0.11", {"start": v(23.95, 11) * mm, "mid": v(23.77, 10.93) * mm, "end": v(23.7, 10.75) * mm});
            skArc(sketch, "E13.20.0.12", {"start": v(23.4, 7) * mm, "mid": v(23.61, 7.09) * mm, "end": v(23.7, 7.3) * mm});
            skArc(sketch, "E13.20.0.13", {"start": v(24.3, 7.3) * mm, "mid": v(24.39, 7.09) * mm, "end": v(24.6, 7) * mm});
            skLineSegment(sketch, "E13.20.0.14", {"start": v(23.95, 11) * mm, "end": v(24.05, 11) * mm});
            skLineSegment(sketch, "E13.21.0.0", {"start": v(25.8, 0) * mm, "end": v(24.6, 0) * mm});
            skPoint(sketch, "E13.21.0.1", {"position": v(25.5, 7) * mm});
            skLineSegment(sketch, "E13.21.0.2", {"start": v(25.8, 7) * mm, "end": v(25.8, 0) * mm});
            skLineSegment(sketch, "E13.21.0.3", {"start": v(25.5, 10.75) * mm, "end": v(25.5, 7.3) * mm});
            skPoint(sketch, "E13.21.0.4", {"position": v(25.5, 11) * mm});
            skPoint(sketch, "E13.21.0.5", {"position": v(24.9, 7) * mm});
            skLineSegment(sketch, "E13.21.0.6", {"start": v(24.6, 0) * mm, "end": v(24.6, 7) * mm});
            skPoint(sketch, "E13.21.0.7", {"position": v(24.9, 11) * mm});
            skLineSegment(sketch, "E13.21.0.8", {"start": v(24.9, 7.3) * mm, "end": v(24.9, 10.75) * mm});
            skArc(sketch, "E13.21.0.9", {"start": v(25.5, 10.75) * mm, "mid": v(25.43, 10.93) * mm, "end": v(25.25, 11) * mm});
            skLineSegment(sketch, "E13.21.0.10", {"start": v(17.9, 0) * mm, "end": v(24.6, 0) * mm, "construction": true});
            skArc(sketch, "E13.21.0.11", {"start": v(25.15, 11) * mm, "mid": v(24.97, 10.93) * mm, "end": v(24.9, 10.75) * mm});
            skArc(sketch, "E13.21.0.12", {"start": v(24.6, 7) * mm, "mid": v(24.81, 7.09) * mm, "end": v(24.9, 7.3) * mm});
            skArc(sketch, "E13.21.0.13", {"start": v(25.5, 7.3) * mm, "mid": v(25.59, 7.09) * mm, "end": v(25.8, 7) * mm});
            skLineSegment(sketch, "E13.21.0.14", {"start": v(25.15, 11) * mm, "end": v(25.25, 11) * mm});
            skLineSegment(sketch, "E13.22.0.0", {"start": v(27, 0) * mm, "end": v(25.8, 0) * mm});
            skPoint(sketch, "E13.22.0.1", {"position": v(26.7, 7) * mm});
            skLineSegment(sketch, "E13.22.0.2", {"start": v(27, 7) * mm, "end": v(27, 0) * mm});
            skLineSegment(sketch, "E13.22.0.3", {"start": v(26.7, 10.75) * mm, "end": v(26.7, 7.3) * mm});
            skPoint(sketch, "E13.22.0.4", {"position": v(26.7, 11) * mm});
            skPoint(sketch, "E13.22.0.5", {"position": v(26.1, 7) * mm});
            skLineSegment(sketch, "E13.22.0.6", {"start": v(25.8, 0) * mm, "end": v(25.8, 7) * mm});
            skPoint(sketch, "E13.22.0.7", {"position": v(26.1, 11) * mm});
            skLineSegment(sketch, "E13.22.0.8", {"start": v(26.1, 7.3) * mm, "end": v(26.1, 10.75) * mm});
            skArc(sketch, "E13.22.0.9", {"start": v(26.7, 10.75) * mm, "mid": v(26.63, 10.93) * mm, "end": v(26.45, 11) * mm});
            skLineSegment(sketch, "E13.22.0.10", {"start": v(19.1, 0) * mm, "end": v(25.8, 0) * mm, "construction": true});
            skArc(sketch, "E13.22.0.11", {"start": v(26.35, 11) * mm, "mid": v(26.17, 10.93) * mm, "end": v(26.1, 10.75) * mm});
            skArc(sketch, "E13.22.0.12", {"start": v(25.8, 7) * mm, "mid": v(26.01, 7.09) * mm, "end": v(26.1, 7.3) * mm});
            skArc(sketch, "E13.22.0.13", {"start": v(26.7, 7.3) * mm, "mid": v(26.79, 7.09) * mm, "end": v(27, 7) * mm});
            skLineSegment(sketch, "E13.22.0.14", {"start": v(26.35, 11) * mm, "end": v(26.45, 11) * mm});
            skLineSegment(sketch, "E13.23.0.0", {"start": v(28.2, 0) * mm, "end": v(27, 0) * mm});
            skPoint(sketch, "E13.23.0.1", {"position": v(27.9, 7) * mm});
            skLineSegment(sketch, "E13.23.0.2", {"start": v(28.2, 7) * mm, "end": v(28.2, 0) * mm});
            skLineSegment(sketch, "E13.23.0.3", {"start": v(27.9, 10.75) * mm, "end": v(27.9, 7.3) * mm});
            skPoint(sketch, "E13.23.0.4", {"position": v(27.9, 11) * mm});
            skPoint(sketch, "E13.23.0.5", {"position": v(27.3, 7) * mm});
            skLineSegment(sketch, "E13.23.0.6", {"start": v(27, 0) * mm, "end": v(27, 7) * mm});
            skPoint(sketch, "E13.23.0.7", {"position": v(27.3, 11) * mm});
            skLineSegment(sketch, "E13.23.0.8", {"start": v(27.3, 7.3) * mm, "end": v(27.3, 10.75) * mm});
            skArc(sketch, "E13.23.0.9", {"start": v(27.9, 10.75) * mm, "mid": v(27.83, 10.93) * mm, "end": v(27.65, 11) * mm});
            skLineSegment(sketch, "E13.23.0.10", {"start": v(20.3, 0) * mm, "end": v(27, 0) * mm, "construction": true});
            skArc(sketch, "E13.23.0.11", {"start": v(27.55, 11) * mm, "mid": v(27.37, 10.93) * mm, "end": v(27.3, 10.75) * mm});
            skArc(sketch, "E13.23.0.12", {"start": v(27, 7) * mm, "mid": v(27.21, 7.09) * mm, "end": v(27.3, 7.3) * mm});
            skArc(sketch, "E13.23.0.13", {"start": v(27.9, 7.3) * mm, "mid": v(27.99, 7.09) * mm, "end": v(28.2, 7) * mm});
            skLineSegment(sketch, "E13.23.0.14", {"start": v(27.55, 11) * mm, "end": v(27.65, 11) * mm});
            skLineSegment(sketch, "E13.24.0.0", {"start": v(29.4, 0) * mm, "end": v(28.2, 0) * mm});
            skPoint(sketch, "E13.24.0.1", {"position": v(29.1, 7) * mm});
            skLineSegment(sketch, "E13.24.0.2", {"start": v(29.4, 7) * mm, "end": v(29.4, 0) * mm});
            skLineSegment(sketch, "E13.24.0.3", {"start": v(29.1, 10.75) * mm, "end": v(29.1, 7.3) * mm});
            skPoint(sketch, "E13.24.0.4", {"position": v(29.1, 11) * mm});
            skPoint(sketch, "E13.24.0.5", {"position": v(28.5, 7) * mm});
            skLineSegment(sketch, "E13.24.0.6", {"start": v(28.2, 0) * mm, "end": v(28.2, 7) * mm});
            skPoint(sketch, "E13.24.0.7", {"position": v(28.5, 11) * mm});
            skLineSegment(sketch, "E13.24.0.8", {"start": v(28.5, 7.3) * mm, "end": v(28.5, 10.75) * mm});
            skArc(sketch, "E13.24.0.9", {"start": v(29.1, 10.75) * mm, "mid": v(29.03, 10.93) * mm, "end": v(28.85, 11) * mm});
            skLineSegment(sketch, "E13.24.0.10", {"start": v(21.5, 0) * mm, "end": v(28.2, 0) * mm, "construction": true});
            skArc(sketch, "E13.24.0.11", {"start": v(28.75, 11) * mm, "mid": v(28.57, 10.93) * mm, "end": v(28.5, 10.75) * mm});
            skArc(sketch, "E13.24.0.12", {"start": v(28.2, 7) * mm, "mid": v(28.41, 7.09) * mm, "end": v(28.5, 7.3) * mm});
            skArc(sketch, "E13.24.0.13", {"start": v(29.1, 7.3) * mm, "mid": v(29.19, 7.09) * mm, "end": v(29.4, 7) * mm});
            skLineSegment(sketch, "E13.24.0.14", {"start": v(28.75, 11) * mm, "end": v(28.85, 11) * mm});
            skLineSegment(sketch, "E13.25.0.0", {"start": v(30.6, 0) * mm, "end": v(29.4, 0) * mm});
            skPoint(sketch, "E13.25.0.1", {"position": v(30.3, 7) * mm});
            skLineSegment(sketch, "E13.25.0.2", {"start": v(30.6, 7) * mm, "end": v(30.6, 0) * mm});
            skLineSegment(sketch, "E13.25.0.3", {"start": v(30.3, 10.75) * mm, "end": v(30.3, 7.3) * mm});
            skPoint(sketch, "E13.25.0.4", {"position": v(30.3, 11) * mm});
            skPoint(sketch, "E13.25.0.5", {"position": v(29.7, 7) * mm});
            skLineSegment(sketch, "E13.25.0.6", {"start": v(29.4, 0) * mm, "end": v(29.4, 7) * mm});
            skPoint(sketch, "E13.25.0.7", {"position": v(29.7, 11) * mm});
            skLineSegment(sketch, "E13.25.0.8", {"start": v(29.7, 7.3) * mm, "end": v(29.7, 10.75) * mm});
            skArc(sketch, "E13.25.0.9", {"start": v(30.3, 10.75) * mm, "mid": v(30.23, 10.93) * mm, "end": v(30.05, 11) * mm});
            skLineSegment(sketch, "E13.25.0.10", {"start": v(22.7, 0) * mm, "end": v(29.4, 0) * mm, "construction": true});
            skArc(sketch, "E13.25.0.11", {"start": v(29.95, 11) * mm, "mid": v(29.77, 10.93) * mm, "end": v(29.7, 10.75) * mm});
            skArc(sketch, "E13.25.0.12", {"start": v(29.4, 7) * mm, "mid": v(29.61, 7.09) * mm, "end": v(29.7, 7.3) * mm});
            skArc(sketch, "E13.25.0.13", {"start": v(30.3, 7.3) * mm, "mid": v(30.39, 7.09) * mm, "end": v(30.6, 7) * mm});
            skLineSegment(sketch, "E13.25.0.14", {"start": v(29.95, 11) * mm, "end": v(30.05, 11) * mm});
            skLineSegment(sketch, "E13.26.0.0", {"start": v(31.8, 0) * mm, "end": v(30.6, 0) * mm});
            skPoint(sketch, "E13.26.0.1", {"position": v(31.5, 7) * mm});
            skLineSegment(sketch, "E13.26.0.2", {"start": v(31.8, 7) * mm, "end": v(31.8, 0) * mm});
            skLineSegment(sketch, "E13.26.0.3", {"start": v(31.5, 10.75) * mm, "end": v(31.5, 7.3) * mm});
            skPoint(sketch, "E13.26.0.4", {"position": v(31.5, 11) * mm});
            skPoint(sketch, "E13.26.0.5", {"position": v(30.9, 7) * mm});
            skLineSegment(sketch, "E13.26.0.6", {"start": v(30.6, 0) * mm, "end": v(30.6, 7) * mm});
            skPoint(sketch, "E13.26.0.7", {"position": v(30.9, 11) * mm});
            skLineSegment(sketch, "E13.26.0.8", {"start": v(30.9, 7.3) * mm, "end": v(30.9, 10.75) * mm});
            skArc(sketch, "E13.26.0.9", {"start": v(31.5, 10.75) * mm, "mid": v(31.43, 10.93) * mm, "end": v(31.25, 11) * mm});
            skLineSegment(sketch, "E13.26.0.10", {"start": v(23.9, 0) * mm, "end": v(30.6, 0) * mm, "construction": true});
            skArc(sketch, "E13.26.0.11", {"start": v(31.15, 11) * mm, "mid": v(30.97, 10.93) * mm, "end": v(30.9, 10.75) * mm});
            skArc(sketch, "E13.26.0.12", {"start": v(30.6, 7) * mm, "mid": v(30.81, 7.09) * mm, "end": v(30.9, 7.3) * mm});
            skArc(sketch, "E13.26.0.13", {"start": v(31.5, 7.3) * mm, "mid": v(31.59, 7.09) * mm, "end": v(31.8, 7) * mm});
            skLineSegment(sketch, "E13.26.0.14", {"start": v(31.15, 11) * mm, "end": v(31.25, 11) * mm});
            skLineSegment(sketch, "E13.27.0.0", {"start": v(33, 0) * mm, "end": v(31.8, 0) * mm});
            skPoint(sketch, "E13.27.0.1", {"position": v(32.7, 7) * mm});
            skLineSegment(sketch, "E13.27.0.2", {"start": v(33, 7) * mm, "end": v(33, 0) * mm});
            skLineSegment(sketch, "E13.27.0.3", {"start": v(32.7, 10.75) * mm, "end": v(32.7, 7.3) * mm});
            skPoint(sketch, "E13.27.0.4", {"position": v(32.7, 11) * mm});
            skPoint(sketch, "E13.27.0.5", {"position": v(32.1, 7) * mm});
            skLineSegment(sketch, "E13.27.0.6", {"start": v(31.8, 0) * mm, "end": v(31.8, 7) * mm});
            skPoint(sketch, "E13.27.0.7", {"position": v(32.1, 11) * mm});
            skLineSegment(sketch, "E13.27.0.8", {"start": v(32.1, 7.3) * mm, "end": v(32.1, 10.75) * mm});
            skArc(sketch, "E13.27.0.9", {"start": v(32.7, 10.75) * mm, "mid": v(32.63, 10.93) * mm, "end": v(32.45, 11) * mm});
            skLineSegment(sketch, "E13.27.0.10", {"start": v(25.1, 0) * mm, "end": v(31.8, 0) * mm, "construction": true});
            skArc(sketch, "E13.27.0.11", {"start": v(32.35, 11) * mm, "mid": v(32.17, 10.93) * mm, "end": v(32.1, 10.75) * mm});
            skArc(sketch, "E13.27.0.12", {"start": v(31.8, 7) * mm, "mid": v(32.01, 7.09) * mm, "end": v(32.1, 7.3) * mm});
            skArc(sketch, "E13.27.0.13", {"start": v(32.7, 7.3) * mm, "mid": v(32.79, 7.09) * mm, "end": v(33, 7) * mm});
            skLineSegment(sketch, "E13.27.0.14", {"start": v(32.35, 11) * mm, "end": v(32.45, 11) * mm});
            skLineSegment(sketch, "E13.28.0.0", {"start": v(34.2, 0) * mm, "end": v(33, 0) * mm});
            skPoint(sketch, "E13.28.0.1", {"position": v(33.9, 7) * mm});
            skLineSegment(sketch, "E13.28.0.2", {"start": v(34.2, 7) * mm, "end": v(34.2, 0) * mm});
            skLineSegment(sketch, "E13.28.0.3", {"start": v(33.9, 10.75) * mm, "end": v(33.9, 7.3) * mm});
            skPoint(sketch, "E13.28.0.4", {"position": v(33.9, 11) * mm});
            skPoint(sketch, "E13.28.0.5", {"position": v(33.3, 7) * mm});
            skLineSegment(sketch, "E13.28.0.6", {"start": v(33, 0) * mm, "end": v(33, 7) * mm});
            skPoint(sketch, "E13.28.0.7", {"position": v(33.3, 11) * mm});
            skLineSegment(sketch, "E13.28.0.8", {"start": v(33.3, 7.3) * mm, "end": v(33.3, 10.75) * mm});
            skArc(sketch, "E13.28.0.9", {"start": v(33.9, 10.75) * mm, "mid": v(33.83, 10.93) * mm, "end": v(33.65, 11) * mm});
            skLineSegment(sketch, "E13.28.0.10", {"start": v(26.3, 0) * mm, "end": v(33, 0) * mm, "construction": true});
            skArc(sketch, "E13.28.0.11", {"start": v(33.55, 11) * mm, "mid": v(33.37, 10.93) * mm, "end": v(33.3, 10.75) * mm});
            skArc(sketch, "E13.28.0.12", {"start": v(33, 7) * mm, "mid": v(33.21, 7.09) * mm, "end": v(33.3, 7.3) * mm});
            skArc(sketch, "E13.28.0.13", {"start": v(33.9, 7.3) * mm, "mid": v(33.99, 7.09) * mm, "end": v(34.2, 7) * mm});
            skLineSegment(sketch, "E13.28.0.14", {"start": v(33.55, 11) * mm, "end": v(33.65, 11) * mm});
            skLineSegment(sketch, "E13.29.0.0", {"start": v(35.4, 0) * mm, "end": v(34.2, 0) * mm});
            skPoint(sketch, "E13.29.0.1", {"position": v(35.1, 7) * mm});
            skLineSegment(sketch, "E13.29.0.2", {"start": v(35.4, 7) * mm, "end": v(35.4, 0) * mm});
            skLineSegment(sketch, "E13.29.0.3", {"start": v(35.1, 10.75) * mm, "end": v(35.1, 7.3) * mm});
            skPoint(sketch, "E13.29.0.4", {"position": v(35.1, 11) * mm});
            skPoint(sketch, "E13.29.0.5", {"position": v(34.5, 7) * mm});
            skLineSegment(sketch, "E13.29.0.6", {"start": v(34.2, 0) * mm, "end": v(34.2, 7) * mm});
            skPoint(sketch, "E13.29.0.7", {"position": v(34.5, 11) * mm});
            skLineSegment(sketch, "E13.29.0.8", {"start": v(34.5, 7.3) * mm, "end": v(34.5, 10.75) * mm});
            skArc(sketch, "E13.29.0.9", {"start": v(35.1, 10.75) * mm, "mid": v(35.03, 10.93) * mm, "end": v(34.85, 11) * mm});
            skLineSegment(sketch, "E13.29.0.10", {"start": v(27.5, 0) * mm, "end": v(34.2, 0) * mm, "construction": true});
            skArc(sketch, "E13.29.0.11", {"start": v(34.75, 11) * mm, "mid": v(34.57, 10.93) * mm, "end": v(34.5, 10.75) * mm});
            skArc(sketch, "E13.29.0.12", {"start": v(34.2, 7) * mm, "mid": v(34.41, 7.09) * mm, "end": v(34.5, 7.3) * mm});
            skArc(sketch, "E13.29.0.13", {"start": v(35.1, 7.3) * mm, "mid": v(35.19, 7.09) * mm, "end": v(35.4, 7) * mm});
            skLineSegment(sketch, "E13.29.0.14", {"start": v(34.75, 11) * mm, "end": v(34.85, 11) * mm});
            skLineSegment(sketch, "E13.30.0.0", {"start": v(36.6, 0) * mm, "end": v(35.4, 0) * mm});
            skPoint(sketch, "E13.30.0.1", {"position": v(36.3, 7) * mm});
            skLineSegment(sketch, "E13.30.0.2", {"start": v(36.6, 7) * mm, "end": v(36.6, 0) * mm});
            skLineSegment(sketch, "E13.30.0.3", {"start": v(36.3, 10.75) * mm, "end": v(36.3, 7.3) * mm});
            skPoint(sketch, "E13.30.0.4", {"position": v(36.3, 11) * mm});
            skPoint(sketch, "E13.30.0.5", {"position": v(35.7, 7) * mm});
            skLineSegment(sketch, "E13.30.0.6", {"start": v(35.4, 0) * mm, "end": v(35.4, 7) * mm});
            skPoint(sketch, "E13.30.0.7", {"position": v(35.7, 11) * mm});
            skLineSegment(sketch, "E13.30.0.8", {"start": v(35.7, 7.3) * mm, "end": v(35.7, 10.75) * mm});
            skArc(sketch, "E13.30.0.9", {"start": v(36.3, 10.75) * mm, "mid": v(36.23, 10.93) * mm, "end": v(36.05, 11) * mm});
            skLineSegment(sketch, "E13.30.0.10", {"start": v(28.7, 0) * mm, "end": v(35.4, 0) * mm, "construction": true});
            skArc(sketch, "E13.30.0.11", {"start": v(35.95, 11) * mm, "mid": v(35.77, 10.93) * mm, "end": v(35.7, 10.75) * mm});
            skArc(sketch, "E13.30.0.12", {"start": v(35.4, 7) * mm, "mid": v(35.61, 7.09) * mm, "end": v(35.7, 7.3) * mm});
            skArc(sketch, "E13.30.0.13", {"start": v(36.3, 7.3) * mm, "mid": v(36.39, 7.09) * mm, "end": v(36.6, 7) * mm});
            skLineSegment(sketch, "E13.30.0.14", {"start": v(35.95, 11) * mm, "end": v(36.05, 11) * mm});
            skLineSegment(sketch, "E13.31.0.0", {"start": v(37.8, 0) * mm, "end": v(36.6, 0) * mm});
            skPoint(sketch, "E13.31.0.1", {"position": v(37.5, 7) * mm});
            skLineSegment(sketch, "E13.31.0.2", {"start": v(37.8, 7) * mm, "end": v(37.8, 0) * mm});
            skLineSegment(sketch, "E13.31.0.3", {"start": v(37.5, 10.75) * mm, "end": v(37.5, 7.3) * mm});
            skPoint(sketch, "E13.31.0.4", {"position": v(37.5, 11) * mm});
            skPoint(sketch, "E13.31.0.5", {"position": v(36.9, 7) * mm});
            skLineSegment(sketch, "E13.31.0.6", {"start": v(36.6, 0) * mm, "end": v(36.6, 7) * mm});
            skPoint(sketch, "E13.31.0.7", {"position": v(36.9, 11) * mm});
            skLineSegment(sketch, "E13.31.0.8", {"start": v(36.9, 7.3) * mm, "end": v(36.9, 10.75) * mm});
            skArc(sketch, "E13.31.0.9", {"start": v(37.5, 10.75) * mm, "mid": v(37.43, 10.93) * mm, "end": v(37.25, 11) * mm});
            skLineSegment(sketch, "E13.31.0.10", {"start": v(29.9, 0) * mm, "end": v(36.6, 0) * mm, "construction": true});
            skArc(sketch, "E13.31.0.11", {"start": v(37.15, 11) * mm, "mid": v(36.97, 10.93) * mm, "end": v(36.9, 10.75) * mm});
            skArc(sketch, "E13.31.0.12", {"start": v(36.6, 7) * mm, "mid": v(36.81, 7.09) * mm, "end": v(36.9, 7.3) * mm});
            skArc(sketch, "E13.31.0.13", {"start": v(37.5, 7.3) * mm, "mid": v(37.59, 7.09) * mm, "end": v(37.8, 7) * mm});
            skLineSegment(sketch, "E13.31.0.14", {"start": v(37.15, 11) * mm, "end": v(37.25, 11) * mm});
            skLineSegment(sketch, "E13.32.0.0", {"start": v(39, 0) * mm, "end": v(37.8, 0) * mm});
            skPoint(sketch, "E13.32.0.1", {"position": v(38.7, 7) * mm});
            skLineSegment(sketch, "E13.32.0.2", {"start": v(39, 7) * mm, "end": v(39, 0) * mm});
            skLineSegment(sketch, "E13.32.0.3", {"start": v(38.7, 10.75) * mm, "end": v(38.7, 7.3) * mm});
            skPoint(sketch, "E13.32.0.4", {"position": v(38.7, 11) * mm});
            skPoint(sketch, "E13.32.0.5", {"position": v(38.1, 7) * mm});
            skLineSegment(sketch, "E13.32.0.6", {"start": v(37.8, 0) * mm, "end": v(37.8, 7) * mm});
            skPoint(sketch, "E13.32.0.7", {"position": v(38.1, 11) * mm});
            skLineSegment(sketch, "E13.32.0.8", {"start": v(38.1, 7.3) * mm, "end": v(38.1, 10.75) * mm});
            skArc(sketch, "E13.32.0.9", {"start": v(38.7, 10.75) * mm, "mid": v(38.63, 10.93) * mm, "end": v(38.45, 11) * mm});
            skLineSegment(sketch, "E13.32.0.10", {"start": v(31.1, 0) * mm, "end": v(37.8, 0) * mm, "construction": true});
            skArc(sketch, "E13.32.0.11", {"start": v(38.35, 11) * mm, "mid": v(38.17, 10.93) * mm, "end": v(38.1, 10.75) * mm});
            skArc(sketch, "E13.32.0.12", {"start": v(37.8, 7) * mm, "mid": v(38.01, 7.09) * mm, "end": v(38.1, 7.3) * mm});
            skArc(sketch, "E13.32.0.13", {"start": v(38.7, 7.3) * mm, "mid": v(38.79, 7.09) * mm, "end": v(39, 7) * mm});
            skLineSegment(sketch, "E13.32.0.14", {"start": v(38.35, 11) * mm, "end": v(38.45, 11) * mm});
            skLineSegment(sketch, "E13.33.0.0", {"start": v(40.2, 0) * mm, "end": v(39, 0) * mm});
            skPoint(sketch, "E13.33.0.1", {"position": v(39.9, 7) * mm});
            skLineSegment(sketch, "E13.33.0.2", {"start": v(40.2, 7) * mm, "end": v(40.2, 0) * mm});
            skLineSegment(sketch, "E13.33.0.3", {"start": v(39.9, 10.75) * mm, "end": v(39.9, 7.3) * mm});
            skPoint(sketch, "E13.33.0.4", {"position": v(39.9, 11) * mm});
            skPoint(sketch, "E13.33.0.5", {"position": v(39.3, 7) * mm});
            skLineSegment(sketch, "E13.33.0.6", {"start": v(39, 0) * mm, "end": v(39, 7) * mm});
            skPoint(sketch, "E13.33.0.7", {"position": v(39.3, 11) * mm});
            skLineSegment(sketch, "E13.33.0.8", {"start": v(39.3, 7.3) * mm, "end": v(39.3, 10.75) * mm});
            skArc(sketch, "E13.33.0.9", {"start": v(39.9, 10.75) * mm, "mid": v(39.83, 10.93) * mm, "end": v(39.65, 11) * mm});
            skLineSegment(sketch, "E13.33.0.10", {"start": v(32.3, 0) * mm, "end": v(39, 0) * mm, "construction": true});
            skArc(sketch, "E13.33.0.11", {"start": v(39.55, 11) * mm, "mid": v(39.37, 10.93) * mm, "end": v(39.3, 10.75) * mm});
            skArc(sketch, "E13.33.0.12", {"start": v(39, 7) * mm, "mid": v(39.21, 7.09) * mm, "end": v(39.3, 7.3) * mm});
            skArc(sketch, "E13.33.0.13", {"start": v(39.9, 7.3) * mm, "mid": v(39.99, 7.09) * mm, "end": v(40.2, 7) * mm});
            skLineSegment(sketch, "E13.33.0.14", {"start": v(39.55, 11) * mm, "end": v(39.65, 11) * mm});
            skLineSegment(sketch, "E13.34.0.0", {"start": v(41.4, 0) * mm, "end": v(40.2, 0) * mm});
            skPoint(sketch, "E13.34.0.1", {"position": v(41.1, 7) * mm});
            skLineSegment(sketch, "E13.34.0.2", {"start": v(41.4, 7) * mm, "end": v(41.4, 0) * mm});
            skLineSegment(sketch, "E13.34.0.3", {"start": v(41.1, 10.75) * mm, "end": v(41.1, 7.3) * mm});
            skPoint(sketch, "E13.34.0.4", {"position": v(41.1, 11) * mm});
            skPoint(sketch, "E13.34.0.5", {"position": v(40.5, 7) * mm});
            skLineSegment(sketch, "E13.34.0.6", {"start": v(40.2, 0) * mm, "end": v(40.2, 7) * mm});
            skPoint(sketch, "E13.34.0.7", {"position": v(40.5, 11) * mm});
            skLineSegment(sketch, "E13.34.0.8", {"start": v(40.5, 7.3) * mm, "end": v(40.5, 10.75) * mm});
            skArc(sketch, "E13.34.0.9", {"start": v(41.1, 10.75) * mm, "mid": v(41.03, 10.93) * mm, "end": v(40.85, 11) * mm});
            skLineSegment(sketch, "E13.34.0.10", {"start": v(33.5, 0) * mm, "end": v(40.2, 0) * mm, "construction": true});
            skArc(sketch, "E13.34.0.11", {"start": v(40.75, 11) * mm, "mid": v(40.57, 10.93) * mm, "end": v(40.5, 10.75) * mm});
            skArc(sketch, "E13.34.0.12", {"start": v(40.2, 7) * mm, "mid": v(40.41, 7.09) * mm, "end": v(40.5, 7.3) * mm});
            skArc(sketch, "E13.34.0.13", {"start": v(41.1, 7.3) * mm, "mid": v(41.19, 7.09) * mm, "end": v(41.4, 7) * mm});
            skLineSegment(sketch, "E13.34.0.14", {"start": v(40.75, 11) * mm, "end": v(40.85, 11) * mm});
            skLineSegment(sketch, "E13.35.0.0", {"start": v(42.6, 0) * mm, "end": v(41.4, 0) * mm});
            skPoint(sketch, "E13.35.0.1", {"position": v(42.3, 7) * mm});
            skLineSegment(sketch, "E13.35.0.2", {"start": v(42.6, 7) * mm, "end": v(42.6, 0) * mm});
            skLineSegment(sketch, "E13.35.0.3", {"start": v(42.3, 10.75) * mm, "end": v(42.3, 7.3) * mm});
            skPoint(sketch, "E13.35.0.4", {"position": v(42.3, 11) * mm});
            skPoint(sketch, "E13.35.0.5", {"position": v(41.7, 7) * mm});
            skLineSegment(sketch, "E13.35.0.6", {"start": v(41.4, 0) * mm, "end": v(41.4, 7) * mm});
            skPoint(sketch, "E13.35.0.7", {"position": v(41.7, 11) * mm});
            skLineSegment(sketch, "E13.35.0.8", {"start": v(41.7, 7.3) * mm, "end": v(41.7, 10.75) * mm});
            skArc(sketch, "E13.35.0.9", {"start": v(42.3, 10.75) * mm, "mid": v(42.23, 10.93) * mm, "end": v(42.05, 11) * mm});
            skLineSegment(sketch, "E13.35.0.10", {"start": v(34.7, 0) * mm, "end": v(41.4, 0) * mm, "construction": true});
            skArc(sketch, "E13.35.0.11", {"start": v(41.95, 11) * mm, "mid": v(41.77, 10.93) * mm, "end": v(41.7, 10.75) * mm});
            skArc(sketch, "E13.35.0.12", {"start": v(41.4, 7) * mm, "mid": v(41.61, 7.09) * mm, "end": v(41.7, 7.3) * mm});
            skArc(sketch, "E13.35.0.13", {"start": v(42.3, 7.3) * mm, "mid": v(42.39, 7.09) * mm, "end": v(42.6, 7) * mm});
            skLineSegment(sketch, "E13.35.0.14", {"start": v(41.95, 11) * mm, "end": v(42.05, 11) * mm});
            skLineSegment(sketch, "E13.36.0.0", {"start": v(43.8, 0) * mm, "end": v(42.6, 0) * mm});
            skPoint(sketch, "E13.36.0.1", {"position": v(43.5, 7) * mm});
            skLineSegment(sketch, "E13.36.0.2", {"start": v(43.8, 7) * mm, "end": v(43.8, 0) * mm});
            skLineSegment(sketch, "E13.36.0.3", {"start": v(43.5, 10.75) * mm, "end": v(43.5, 7.3) * mm});
            skPoint(sketch, "E13.36.0.4", {"position": v(43.5, 11) * mm});
            skPoint(sketch, "E13.36.0.5", {"position": v(42.9, 7) * mm});
            skLineSegment(sketch, "E13.36.0.6", {"start": v(42.6, 0) * mm, "end": v(42.6, 7) * mm});
            skPoint(sketch, "E13.36.0.7", {"position": v(42.9, 11) * mm});
            skLineSegment(sketch, "E13.36.0.8", {"start": v(42.9, 7.3) * mm, "end": v(42.9, 10.75) * mm});
            skArc(sketch, "E13.36.0.9", {"start": v(43.5, 10.75) * mm, "mid": v(43.43, 10.93) * mm, "end": v(43.25, 11) * mm});
            skLineSegment(sketch, "E13.36.0.10", {"start": v(35.9, 0) * mm, "end": v(42.6, 0) * mm, "construction": true});
            skArc(sketch, "E13.36.0.11", {"start": v(43.15, 11) * mm, "mid": v(42.97, 10.93) * mm, "end": v(42.9, 10.75) * mm});
            skArc(sketch, "E13.36.0.12", {"start": v(42.6, 7) * mm, "mid": v(42.81, 7.09) * mm, "end": v(42.9, 7.3) * mm});
            skArc(sketch, "E13.36.0.13", {"start": v(43.5, 7.3) * mm, "mid": v(43.59, 7.09) * mm, "end": v(43.8, 7) * mm});
            skLineSegment(sketch, "E13.36.0.14", {"start": v(43.15, 11) * mm, "end": v(43.25, 11) * mm});
            skLineSegment(sketch, "E13.37.0.0", {"start": v(45, 0) * mm, "end": v(43.8, 0) * mm});
            skPoint(sketch, "E13.37.0.1", {"position": v(44.7, 7) * mm});
            skLineSegment(sketch, "E13.37.0.2", {"start": v(45, 7) * mm, "end": v(45, 0) * mm});
            skLineSegment(sketch, "E13.37.0.3", {"start": v(44.7, 10.75) * mm, "end": v(44.7, 7.3) * mm});
            skPoint(sketch, "E13.37.0.4", {"position": v(44.7, 11) * mm});
            skPoint(sketch, "E13.37.0.5", {"position": v(44.1, 7) * mm});
            skLineSegment(sketch, "E13.37.0.6", {"start": v(43.8, 0) * mm, "end": v(43.8, 7) * mm});
            skPoint(sketch, "E13.37.0.7", {"position": v(44.1, 11) * mm});
            skLineSegment(sketch, "E13.37.0.8", {"start": v(44.1, 7.3) * mm, "end": v(44.1, 10.75) * mm});
            skArc(sketch, "E13.37.0.9", {"start": v(44.7, 10.75) * mm, "mid": v(44.63, 10.93) * mm, "end": v(44.45, 11) * mm});
            skLineSegment(sketch, "E13.37.0.10", {"start": v(37.1, 0) * mm, "end": v(43.8, 0) * mm, "construction": true});
            skArc(sketch, "E13.37.0.11", {"start": v(44.35, 11) * mm, "mid": v(44.17, 10.93) * mm, "end": v(44.1, 10.75) * mm});
            skArc(sketch, "E13.37.0.12", {"start": v(43.8, 7) * mm, "mid": v(44.01, 7.09) * mm, "end": v(44.1, 7.3) * mm});
            skArc(sketch, "E13.37.0.13", {"start": v(44.7, 7.3) * mm, "mid": v(44.79, 7.09) * mm, "end": v(45, 7) * mm});
            skLineSegment(sketch, "E13.37.0.14", {"start": v(44.35, 11) * mm, "end": v(44.45, 11) * mm});
            skLineSegment(sketch, "E13.38.0.0", {"start": v(46.2, 0) * mm, "end": v(45, 0) * mm});
            skPoint(sketch, "E13.38.0.1", {"position": v(45.9, 7) * mm});
            skLineSegment(sketch, "E13.38.0.2", {"start": v(46.2, 7) * mm, "end": v(46.2, 0) * mm});
            skLineSegment(sketch, "E13.38.0.3", {"start": v(45.9, 10.75) * mm, "end": v(45.9, 7.3) * mm});
            skPoint(sketch, "E13.38.0.4", {"position": v(45.9, 11) * mm});
            skPoint(sketch, "E13.38.0.5", {"position": v(45.3, 7) * mm});
            skLineSegment(sketch, "E13.38.0.6", {"start": v(45, 0) * mm, "end": v(45, 7) * mm});
            skPoint(sketch, "E13.38.0.7", {"position": v(45.3, 11) * mm});
            skLineSegment(sketch, "E13.38.0.8", {"start": v(45.3, 7.3) * mm, "end": v(45.3, 10.75) * mm});
            skArc(sketch, "E13.38.0.9", {"start": v(45.9, 10.75) * mm, "mid": v(45.83, 10.93) * mm, "end": v(45.65, 11) * mm});
            skLineSegment(sketch, "E13.38.0.10", {"start": v(38.3, 0) * mm, "end": v(45, 0) * mm, "construction": true});
            skArc(sketch, "E13.38.0.11", {"start": v(45.55, 11) * mm, "mid": v(45.37, 10.93) * mm, "end": v(45.3, 10.75) * mm});
            skArc(sketch, "E13.38.0.12", {"start": v(45, 7) * mm, "mid": v(45.21, 7.09) * mm, "end": v(45.3, 7.3) * mm});
            skArc(sketch, "E13.38.0.13", {"start": v(45.9, 7.3) * mm, "mid": v(45.99, 7.09) * mm, "end": v(46.2, 7) * mm});
            skLineSegment(sketch, "E13.38.0.14", {"start": v(45.55, 11) * mm, "end": v(45.65, 11) * mm});
            skLineSegment(sketch, "E13.39.0.0", {"start": v(47.4, 0) * mm, "end": v(46.2, 0) * mm});
            skPoint(sketch, "E13.39.0.1", {"position": v(47.1, 7) * mm});
            skLineSegment(sketch, "E13.39.0.2", {"start": v(47.4, 7) * mm, "end": v(47.4, 0) * mm});
            skLineSegment(sketch, "E13.39.0.3", {"start": v(47.1, 10.75) * mm, "end": v(47.1, 7.3) * mm});
            skPoint(sketch, "E13.39.0.4", {"position": v(47.1, 11) * mm});
            skPoint(sketch, "E13.39.0.5", {"position": v(46.5, 7) * mm});
            skLineSegment(sketch, "E13.39.0.6", {"start": v(46.2, 0) * mm, "end": v(46.2, 7) * mm});
            skPoint(sketch, "E13.39.0.7", {"position": v(46.5, 11) * mm});
            skLineSegment(sketch, "E13.39.0.8", {"start": v(46.5, 7.3) * mm, "end": v(46.5, 10.75) * mm});
            skArc(sketch, "E13.39.0.9", {"start": v(47.1, 10.75) * mm, "mid": v(47.03, 10.93) * mm, "end": v(46.85, 11) * mm});
            skLineSegment(sketch, "E13.39.0.10", {"start": v(39.5, 0) * mm, "end": v(46.2, 0) * mm, "construction": true});
            skArc(sketch, "E13.39.0.11", {"start": v(46.75, 11) * mm, "mid": v(46.57, 10.93) * mm, "end": v(46.5, 10.75) * mm});
            skArc(sketch, "E13.39.0.12", {"start": v(46.2, 7) * mm, "mid": v(46.41, 7.09) * mm, "end": v(46.5, 7.3) * mm});
            skArc(sketch, "E13.39.0.13", {"start": v(47.1, 7.3) * mm, "mid": v(47.19, 7.09) * mm, "end": v(47.4, 7) * mm});
            skLineSegment(sketch, "E13.39.0.14", {"start": v(46.75, 11) * mm, "end": v(46.85, 11) * mm});
            skLineSegment(sketch, "E13.direction1", {"start": v(-0.6, 0) * mm, "end": v(0.6, 0) * mm, "construction": true});
            skSolve(sketch);
        }
        {
            var Q0;
            Q0 = qSketchRegion(id + "F0", true);
            extrude(context, id + "F1", {"entities" : qUnion([Q0]), "depth" : 6 * mm, "symmetric" : true});
        }
        {
            var Q0;
            Q0=makeQuery(id+"F1.opExtrude","SWEPT_FACE",FACE,{"disambiguationData":[OSD([sQuery(id+"F0.wireOp",EDGE,"E6"),sQuery(id+"F0.wireOp",EDGE,"E13.1.0.0"),sQuery(id+"F0.wireOp",EDGE,"E13.2.0.0"),sQuery(id+"F0.wireOp",EDGE,"E13.3.0.0"),sQuery(id+"F0.wireOp",EDGE,"E13.4.0.0"),sQuery(id+"F0.wireOp",EDGE,"E13.5.0.0"),sQuery(id+"F0.wireOp",EDGE,"E13.6.0.0"),sQuery(id+"F0.wireOp",EDGE,"E13.7.0.0"),sQuery(id+"F0.wireOp",EDGE,"E13.8.0.0"),sQuery(id+"F0.wireOp",EDGE,"E13.9.0.0"),sQuery(id+"F0.wireOp",EDGE,"E13.10.0.0"),sQuery(id+"F0.wireOp",EDGE,"E13.11.0.0"),sQuery(id+"F0.wireOp",EDGE,"E13.12.0.0"),sQuery(id+"F0.wireOp",EDGE,"E13.13.0.0"),sQuery(id+"F0.wireOp",EDGE,"E13.14.0.0"),sQuery(id+"F0.wireOp",EDGE,"E13.15.0.0"),sQuery(id+"F0.wireOp",EDGE,"E13.16.0.0"),sQuery(id+"F0.wireOp",EDGE,"E13.17.0.0"),sQuery(id+"F0.wireOp",EDGE,"E13.18.0.0"),sQuery(id+"F0.wireOp",EDGE,"E13.19.0.0"),sQuery(id+"F0.wireOp",EDGE,"E13.20.0.0"),sQuery(id+"F0.wireOp",EDGE,"E13.21.0.0"),sQuery(id+"F0.wireOp",EDGE,"E13.22.0.0"),sQuery(id+"F0.wireOp",EDGE,"E13.23.0.0"),sQuery(id+"F0.wireOp",EDGE,"E13.24.0.0"),sQuery(id+"F0.wireOp",EDGE,"E13.25.0.0"),sQuery(id+"F0.wireOp",EDGE,"E13.26.0.0"),sQuery(id+"F0.wireOp",EDGE,"E13.27.0.0"),sQuery(id+"F0.wireOp",EDGE,"E13.28.0.0"),sQuery(id+"F0.wireOp",EDGE,"E13.29.0.0"),sQuery(id+"F0.wireOp",EDGE,"E13.30.0.0"),sQuery(id+"F0.wireOp",EDGE,"E13.31.0.0"),sQuery(id+"F0.wireOp",EDGE,"E13.32.0.0"),sQuery(id+"F0.wireOp",EDGE,"E13.33.0.0"),sQuery(id+"F0.wireOp",EDGE,"E13.34.0.0"),sQuery(id+"F0.wireOp",EDGE,"E13.35.0.0"),sQuery(id+"F0.wireOp",EDGE,"E13.36.0.0"),sQuery(id+"F0.wireOp",EDGE,"E13.37.0.0"),sQuery(id+"F0.wireOp",EDGE,"E13.38.0.0"),sQuery(id+"F0.wireOp",EDGE,"E13.39.0.0")])]});
            var sketch = newSketch(context, id + "F2", { "sketchPlane" : qUnion([Q0])});
            skLineSegment(sketch, "E14.bottom", {"start": v(47.4, -3) * mm, "end": v(47.1, -3) * mm});
            skLineSegment(sketch, "E14.top", {"start": v(47.4, 3) * mm, "end": v(47.1, 3) * mm});
            skLineSegment(sketch, "E14.left", {"start": v(47.4, -3) * mm, "end": v(47.4, 3) * mm});
            skLineSegment(sketch, "E14.right", {"start": v(47.1, -3) * mm, "end": v(47.1, 3) * mm});
            skLineSegment(sketch, "E15.bottom", {"start": v(-0.6, 3) * mm, "end": v(-0.3, 3) * mm});
            skLineSegment(sketch, "E15.top", {"start": v(-0.6, -3) * mm, "end": v(-0.3, -3) * mm});
            skLineSegment(sketch, "E15.left", {"start": v(-0.6, 3) * mm, "end": v(-0.6, -3) * mm});
            skLineSegment(sketch, "E15.right", {"start": v(-0.3, 3) * mm, "end": v(-0.3, -3) * mm});
            skSolve(sketch);
        }
        {
            var Q0;
            Q0=makeQuery(id+"F2.imprint","IMPRINT",FACE,{"disambiguationData":[TD([[makeQuery(id+"F2.imprint","IMPRINT",EDGE,{"derivedFrom":sQuery(id+"F2.wireOp",EDGE,"E14.bottom")}),-1.0]])]});
            var Q1;
            Q1=makeQuery(id+"F2.imprint","IMPRINT",FACE,{"disambiguationData":[TD([[makeQuery(id+"F2.imprint","IMPRINT",EDGE,{"derivedFrom":sQuery(id+"F2.wireOp",EDGE,"E15.bottom")}),1.0]])]});
            extrude(context, id + "F3", {"entities" : qUnion([Q0, Q1]), "operationType" : NewBodyOperationType.REMOVE, "endBound" : BoundingType.THROUGH_ALL, "oppositeDirection" : true, "depth" : 25 * mm});
        }
        {
            var Q0;
            Q0=makeQuery(id+"F1.opExtrude","CAP_FACE",FACE,{"disambiguationData":[OSD([sQuery(id+"F0.wireOp",EDGE,"E1"),sQuery(id+"F0.wireOp",EDGE,"E2"),sQuery(id+"F0.wireOp",EDGE,"E3"),sQuery(id+"F0.wireOp",EDGE,"E6"),sQuery(id+"F0.wireOp",EDGE,"E7"),sQuery(id+"F0.wireOp",EDGE,"E9.filletArc"),sQuery(id+"F0.wireOp",EDGE,"E10.filletArc"),sQuery(id+"F0.wireOp",EDGE,"E11.filletArc"),sQuery(id+"F0.wireOp",EDGE,"E12.filletArc"),sQuery(id+"F0.wireOp",EDGE,"E13.1.0.0"),sQuery(id+"F0.wireOp",EDGE,"E13.1.0.3"),sQuery(id+"F0.wireOp",EDGE,"E13.1.0.8"),sQuery(id+"F0.wireOp",EDGE,"E13.1.0.9"),sQuery(id+"F0.wireOp",EDGE,"E13.1.0.11"),sQuery(id+"F0.wireOp",EDGE,"E13.1.0.12"),sQuery(id+"F0.wireOp",EDGE,"E13.1.0.13"),sQuery(id+"F0.wireOp",EDGE,"E13.1.0.14"),sQuery(id+"F0.wireOp",EDGE,"E13.2.0.0"),sQuery(id+"F0.wireOp",EDGE,"E13.2.0.3"),sQuery(id+"F0.wireOp",EDGE,"E13.2.0.8"),sQuery(id+"F0.wireOp",EDGE,"E13.2.0.9"),sQuery(id+"F0.wireOp",EDGE,"E13.2.0.11"),sQuery(id+"F0.wireOp",EDGE,"E13.2.0.12"),sQuery(id+"F0.wireOp",EDGE,"E13.2.0.13"),sQuery(id+"F0.wireOp",EDGE,"E13.2.0.14"),sQuery(id+"F0.wireOp",EDGE,"E13.3.0.0"),sQuery(id+"F0.wireOp",EDGE,"E13.3.0.3"),sQuery(id+"F0.wireOp",EDGE,"E13.3.0.8"),sQuery(id+"F0.wireOp",EDGE,"E13.3.0.9"),sQuery(id+"F0.wireOp",EDGE,"E13.3.0.11"),sQuery(id+"F0.wireOp",EDGE,"E13.3.0.12"),sQuery(id+"F0.wireOp",EDGE,"E13.3.0.13"),sQuery(id+"F0.wireOp",EDGE,"E13.3.0.14"),sQuery(id+"F0.wireOp",EDGE,"E13.4.0.0"),sQuery(id+"F0.wireOp",EDGE,"E13.4.0.3"),sQuery(id+"F0.wireOp",EDGE,"E13.4.0.8"),sQuery(id+"F0.wireOp",EDGE,"E13.4.0.9"),sQuery(id+"F0.wireOp",EDGE,"E13.4.0.11"),sQuery(id+"F0.wireOp",EDGE,"E13.4.0.12"),sQuery(id+"F0.wireOp",EDGE,"E13.4.0.13"),sQuery(id+"F0.wireOp",EDGE,"E13.4.0.14"),sQuery(id+"F0.wireOp",EDGE,"E13.5.0.0"),sQuery(id+"F0.wireOp",EDGE,"E13.5.0.3"),sQuery(id+"F0.wireOp",EDGE,"E13.5.0.8"),sQuery(id+"F0.wireOp",EDGE,"E13.5.0.9"),sQuery(id+"F0.wireOp",EDGE,"E13.5.0.11"),sQuery(id+"F0.wireOp",EDGE,"E13.5.0.12"),sQuery(id+"F0.wireOp",EDGE,"E13.5.0.13"),sQuery(id+"F0.wireOp",EDGE,"E13.5.0.14"),sQuery(id+"F0.wireOp",EDGE,"E13.6.0.0"),sQuery(id+"F0.wireOp",EDGE,"E13.6.0.3"),sQuery(id+"F0.wireOp",EDGE,"E13.6.0.8"),sQuery(id+"F0.wireOp",EDGE,"E13.6.0.9"),sQuery(id+"F0.wireOp",EDGE,"E13.6.0.11"),sQuery(id+"F0.wireOp",EDGE,"E13.6.0.12"),sQuery(id+"F0.wireOp",EDGE,"E13.6.0.13"),sQuery(id+"F0.wireOp",EDGE,"E13.6.0.14"),sQuery(id+"F0.wireOp",EDGE,"E13.7.0.0"),sQuery(id+"F0.wireOp",EDGE,"E13.7.0.3"),sQuery(id+"F0.wireOp",EDGE,"E13.7.0.8"),sQuery(id+"F0.wireOp",EDGE,"E13.7.0.9"),sQuery(id+"F0.wireOp",EDGE,"E13.7.0.11"),sQuery(id+"F0.wireOp",EDGE,"E13.7.0.12"),sQuery(id+"F0.wireOp",EDGE,"E13.7.0.13"),sQuery(id+"F0.wireOp",EDGE,"E13.7.0.14"),sQuery(id+"F0.wireOp",EDGE,"E13.8.0.0"),sQuery(id+"F0.wireOp",EDGE,"E13.8.0.3"),sQuery(id+"F0.wireOp",EDGE,"E13.8.0.8"),sQuery(id+"F0.wireOp",EDGE,"E13.8.0.9"),sQuery(id+"F0.wireOp",EDGE,"E13.8.0.11"),sQuery(id+"F0.wireOp",EDGE,"E13.8.0.12"),sQuery(id+"F0.wireOp",EDGE,"E13.8.0.13"),sQuery(id+"F0.wireOp",EDGE,"E13.8.0.14"),sQuery(id+"F0.wireOp",EDGE,"E13.9.0.0"),sQuery(id+"F0.wireOp",EDGE,"E13.9.0.3"),sQuery(id+"F0.wireOp",EDGE,"E13.9.0.8"),sQuery(id+"F0.wireOp",EDGE,"E13.9.0.9"),sQuery(id+"F0.wireOp",EDGE,"E13.9.0.11"),sQuery(id+"F0.wireOp",EDGE,"E13.9.0.12"),sQuery(id+"F0.wireOp",EDGE,"E13.9.0.13"),sQuery(id+"F0.wireOp",EDGE,"E13.9.0.14"),sQuery(id+"F0.wireOp",EDGE,"E13.10.0.0"),sQuery(id+"F0.wireOp",EDGE,"E13.10.0.3"),sQuery(id+"F0.wireOp",EDGE,"E13.10.0.8"),sQuery(id+"F0.wireOp",EDGE,"E13.10.0.9"),sQuery(id+"F0.wireOp",EDGE,"E13.10.0.11"),sQuery(id+"F0.wireOp",EDGE,"E13.10.0.12"),sQuery(id+"F0.wireOp",EDGE,"E13.10.0.13"),sQuery(id+"F0.wireOp",EDGE,"E13.10.0.14"),sQuery(id+"F0.wireOp",EDGE,"E13.11.0.0"),sQuery(id+"F0.wireOp",EDGE,"E13.11.0.3"),sQuery(id+"F0.wireOp",EDGE,"E13.11.0.8"),sQuery(id+"F0.wireOp",EDGE,"E13.11.0.9"),sQuery(id+"F0.wireOp",EDGE,"E13.11.0.11"),sQuery(id+"F0.wireOp",EDGE,"E13.11.0.12"),sQuery(id+"F0.wireOp",EDGE,"E13.11.0.13"),sQuery(id+"F0.wireOp",EDGE,"E13.11.0.14"),sQuery(id+"F0.wireOp",EDGE,"E13.12.0.0"),sQuery(id+"F0.wireOp",EDGE,"E13.12.0.3"),sQuery(id+"F0.wireOp",EDGE,"E13.12.0.8"),sQuery(id+"F0.wireOp",EDGE,"E13.12.0.9"),sQuery(id+"F0.wireOp",EDGE,"E13.12.0.11"),sQuery(id+"F0.wireOp",EDGE,"E13.12.0.12"),sQuery(id+"F0.wireOp",EDGE,"E13.12.0.13"),sQuery(id+"F0.wireOp",EDGE,"E13.12.0.14"),sQuery(id+"F0.wireOp",EDGE,"E13.13.0.0"),sQuery(id+"F0.wireOp",EDGE,"E13.13.0.3"),sQuery(id+"F0.wireOp",EDGE,"E13.13.0.8"),sQuery(id+"F0.wireOp",EDGE,"E13.13.0.9"),sQuery(id+"F0.wireOp",EDGE,"E13.13.0.11"),sQuery(id+"F0.wireOp",EDGE,"E13.13.0.12"),sQuery(id+"F0.wireOp",EDGE,"E13.13.0.13"),sQuery(id+"F0.wireOp",EDGE,"E13.13.0.14"),sQuery(id+"F0.wireOp",EDGE,"E13.14.0.0"),sQuery(id+"F0.wireOp",EDGE,"E13.14.0.3"),sQuery(id+"F0.wireOp",EDGE,"E13.14.0.8"),sQuery(id+"F0.wireOp",EDGE,"E13.14.0.9"),sQuery(id+"F0.wireOp",EDGE,"E13.14.0.11"),sQuery(id+"F0.wireOp",EDGE,"E13.14.0.12"),sQuery(id+"F0.wireOp",EDGE,"E13.14.0.13"),sQuery(id+"F0.wireOp",EDGE,"E13.14.0.14"),sQuery(id+"F0.wireOp",EDGE,"E13.15.0.0"),sQuery(id+"F0.wireOp",EDGE,"E13.15.0.3"),sQuery(id+"F0.wireOp",EDGE,"E13.15.0.8"),sQuery(id+"F0.wireOp",EDGE,"E13.15.0.9"),sQuery(id+"F0.wireOp",EDGE,"E13.15.0.11"),sQuery(id+"F0.wireOp",EDGE,"E13.15.0.12"),sQuery(id+"F0.wireOp",EDGE,"E13.15.0.13"),sQuery(id+"F0.wireOp",EDGE,"E13.15.0.14"),sQuery(id+"F0.wireOp",EDGE,"E13.16.0.0"),sQuery(id+"F0.wireOp",EDGE,"E13.16.0.3"),sQuery(id+"F0.wireOp",EDGE,"E13.16.0.8"),sQuery(id+"F0.wireOp",EDGE,"E13.16.0.9"),sQuery(id+"F0.wireOp",EDGE,"E13.16.0.11"),sQuery(id+"F0.wireOp",EDGE,"E13.16.0.12"),sQuery(id+"F0.wireOp",EDGE,"E13.16.0.13"),sQuery(id+"F0.wireOp",EDGE,"E13.16.0.14"),sQuery(id+"F0.wireOp",EDGE,"E13.17.0.0"),sQuery(id+"F0.wireOp",EDGE,"E13.17.0.3"),sQuery(id+"F0.wireOp",EDGE,"E13.17.0.8"),sQuery(id+"F0.wireOp",EDGE,"E13.17.0.9"),sQuery(id+"F0.wireOp",EDGE,"E13.17.0.11"),sQuery(id+"F0.wireOp",EDGE,"E13.17.0.12"),sQuery(id+"F0.wireOp",EDGE,"E13.17.0.13"),sQuery(id+"F0.wireOp",EDGE,"E13.17.0.14"),sQuery(id+"F0.wireOp",EDGE,"E13.18.0.0"),sQuery(id+"F0.wireOp",EDGE,"E13.18.0.3"),sQuery(id+"F0.wireOp",EDGE,"E13.18.0.8"),sQuery(id+"F0.wireOp",EDGE,"E13.18.0.9"),sQuery(id+"F0.wireOp",EDGE,"E13.18.0.11"),sQuery(id+"F0.wireOp",EDGE,"E13.18.0.12"),sQuery(id+"F0.wireOp",EDGE,"E13.18.0.13"),sQuery(id+"F0.wireOp",EDGE,"E13.18.0.14"),sQuery(id+"F0.wireOp",EDGE,"E13.19.0.0"),sQuery(id+"F0.wireOp",EDGE,"E13.19.0.3"),sQuery(id+"F0.wireOp",EDGE,"E13.19.0.8"),sQuery(id+"F0.wireOp",EDGE,"E13.19.0.9"),sQuery(id+"F0.wireOp",EDGE,"E13.19.0.11"),sQuery(id+"F0.wireOp",EDGE,"E13.19.0.12"),sQuery(id+"F0.wireOp",EDGE,"E13.19.0.13"),sQuery(id+"F0.wireOp",EDGE,"E13.19.0.14"),sQuery(id+"F0.wireOp",EDGE,"E13.20.0.0"),sQuery(id+"F0.wireOp",EDGE,"E13.20.0.3"),sQuery(id+"F0.wireOp",EDGE,"E13.20.0.8"),sQuery(id+"F0.wireOp",EDGE,"E13.20.0.9"),sQuery(id+"F0.wireOp",EDGE,"E13.20.0.11"),sQuery(id+"F0.wireOp",EDGE,"E13.20.0.12"),sQuery(id+"F0.wireOp",EDGE,"E13.20.0.13"),sQuery(id+"F0.wireOp",EDGE,"E13.20.0.14"),sQuery(id+"F0.wireOp",EDGE,"E13.21.0.0"),sQuery(id+"F0.wireOp",EDGE,"E13.21.0.3"),sQuery(id+"F0.wireOp",EDGE,"E13.21.0.8"),sQuery(id+"F0.wireOp",EDGE,"E13.21.0.9"),sQuery(id+"F0.wireOp",EDGE,"E13.21.0.11"),sQuery(id+"F0.wireOp",EDGE,"E13.21.0.12"),sQuery(id+"F0.wireOp",EDGE,"E13.21.0.13"),sQuery(id+"F0.wireOp",EDGE,"E13.21.0.14"),sQuery(id+"F0.wireOp",EDGE,"E13.22.0.0"),sQuery(id+"F0.wireOp",EDGE,"E13.22.0.3"),sQuery(id+"F0.wireOp",EDGE,"E13.22.0.8"),sQuery(id+"F0.wireOp",EDGE,"E13.22.0.9"),sQuery(id+"F0.wireOp",EDGE,"E13.22.0.11"),sQuery(id+"F0.wireOp",EDGE,"E13.22.0.12"),sQuery(id+"F0.wireOp",EDGE,"E13.22.0.13"),sQuery(id+"F0.wireOp",EDGE,"E13.22.0.14"),sQuery(id+"F0.wireOp",EDGE,"E13.23.0.0"),sQuery(id+"F0.wireOp",EDGE,"E13.23.0.3"),sQuery(id+"F0.wireOp",EDGE,"E13.23.0.8"),sQuery(id+"F0.wireOp",EDGE,"E13.23.0.9"),sQuery(id+"F0.wireOp",EDGE,"E13.23.0.11"),sQuery(id+"F0.wireOp",EDGE,"E13.23.0.12"),sQuery(id+"F0.wireOp",EDGE,"E13.23.0.13"),sQuery(id+"F0.wireOp",EDGE,"E13.23.0.14"),sQuery(id+"F0.wireOp",EDGE,"E13.24.0.0"),sQuery(id+"F0.wireOp",EDGE,"E13.24.0.3"),sQuery(id+"F0.wireOp",EDGE,"E13.24.0.8"),sQuery(id+"F0.wireOp",EDGE,"E13.24.0.9"),sQuery(id+"F0.wireOp",EDGE,"E13.24.0.11"),sQuery(id+"F0.wireOp",EDGE,"E13.24.0.12"),sQuery(id+"F0.wireOp",EDGE,"E13.24.0.13"),sQuery(id+"F0.wireOp",EDGE,"E13.24.0.14"),sQuery(id+"F0.wireOp",EDGE,"E13.25.0.0"),sQuery(id+"F0.wireOp",EDGE,"E13.25.0.3"),sQuery(id+"F0.wireOp",EDGE,"E13.25.0.8"),sQuery(id+"F0.wireOp",EDGE,"E13.25.0.9"),sQuery(id+"F0.wireOp",EDGE,"E13.25.0.11"),sQuery(id+"F0.wireOp",EDGE,"E13.25.0.12"),sQuery(id+"F0.wireOp",EDGE,"E13.25.0.13"),sQuery(id+"F0.wireOp",EDGE,"E13.25.0.14"),sQuery(id+"F0.wireOp",EDGE,"E13.26.0.0"),sQuery(id+"F0.wireOp",EDGE,"E13.26.0.3"),sQuery(id+"F0.wireOp",EDGE,"E13.26.0.8"),sQuery(id+"F0.wireOp",EDGE,"E13.26.0.9"),sQuery(id+"F0.wireOp",EDGE,"E13.26.0.11"),sQuery(id+"F0.wireOp",EDGE,"E13.26.0.12"),sQuery(id+"F0.wireOp",EDGE,"E13.26.0.13"),sQuery(id+"F0.wireOp",EDGE,"E13.26.0.14"),sQuery(id+"F0.wireOp",EDGE,"E13.27.0.0"),sQuery(id+"F0.wireOp",EDGE,"E13.27.0.3"),sQuery(id+"F0.wireOp",EDGE,"E13.27.0.8"),sQuery(id+"F0.wireOp",EDGE,"E13.27.0.9"),sQuery(id+"F0.wireOp",EDGE,"E13.27.0.11"),sQuery(id+"F0.wireOp",EDGE,"E13.27.0.12"),sQuery(id+"F0.wireOp",EDGE,"E13.27.0.13"),sQuery(id+"F0.wireOp",EDGE,"E13.27.0.14"),sQuery(id+"F0.wireOp",EDGE,"E13.28.0.0"),sQuery(id+"F0.wireOp",EDGE,"E13.28.0.3"),sQuery(id+"F0.wireOp",EDGE,"E13.28.0.8"),sQuery(id+"F0.wireOp",EDGE,"E13.28.0.9"),sQuery(id+"F0.wireOp",EDGE,"E13.28.0.11"),sQuery(id+"F0.wireOp",EDGE,"E13.28.0.12"),sQuery(id+"F0.wireOp",EDGE,"E13.28.0.13"),sQuery(id+"F0.wireOp",EDGE,"E13.28.0.14"),sQuery(id+"F0.wireOp",EDGE,"E13.29.0.0"),sQuery(id+"F0.wireOp",EDGE,"E13.29.0.3"),sQuery(id+"F0.wireOp",EDGE,"E13.29.0.8"),sQuery(id+"F0.wireOp",EDGE,"E13.29.0.9"),sQuery(id+"F0.wireOp",EDGE,"E13.29.0.11"),sQuery(id+"F0.wireOp",EDGE,"E13.29.0.12"),sQuery(id+"F0.wireOp",EDGE,"E13.29.0.13"),sQuery(id+"F0.wireOp",EDGE,"E13.29.0.14"),sQuery(id+"F0.wireOp",EDGE,"E13.30.0.0"),sQuery(id+"F0.wireOp",EDGE,"E13.30.0.3"),sQuery(id+"F0.wireOp",EDGE,"E13.30.0.8"),sQuery(id+"F0.wireOp",EDGE,"E13.30.0.9"),sQuery(id+"F0.wireOp",EDGE,"E13.30.0.11"),sQuery(id+"F0.wireOp",EDGE,"E13.30.0.12"),sQuery(id+"F0.wireOp",EDGE,"E13.30.0.13"),sQuery(id+"F0.wireOp",EDGE,"E13.30.0.14"),sQuery(id+"F0.wireOp",EDGE,"E13.31.0.0"),sQuery(id+"F0.wireOp",EDGE,"E13.31.0.3"),sQuery(id+"F0.wireOp",EDGE,"E13.31.0.8"),sQuery(id+"F0.wireOp",EDGE,"E13.31.0.9"),sQuery(id+"F0.wireOp",EDGE,"E13.31.0.11"),sQuery(id+"F0.wireOp",EDGE,"E13.31.0.12"),sQuery(id+"F0.wireOp",EDGE,"E13.31.0.13"),sQuery(id+"F0.wireOp",EDGE,"E13.31.0.14"),sQuery(id+"F0.wireOp",EDGE,"E13.32.0.0"),sQuery(id+"F0.wireOp",EDGE,"E13.32.0.3"),sQuery(id+"F0.wireOp",EDGE,"E13.32.0.8"),sQuery(id+"F0.wireOp",EDGE,"E13.32.0.9"),sQuery(id+"F0.wireOp",EDGE,"E13.32.0.11"),sQuery(id+"F0.wireOp",EDGE,"E13.32.0.12"),sQuery(id+"F0.wireOp",EDGE,"E13.32.0.13"),sQuery(id+"F0.wireOp",EDGE,"E13.32.0.14"),sQuery(id+"F0.wireOp",EDGE,"E13.33.0.0"),sQuery(id+"F0.wireOp",EDGE,"E13.33.0.3"),sQuery(id+"F0.wireOp",EDGE,"E13.33.0.8"),sQuery(id+"F0.wireOp",EDGE,"E13.33.0.9"),sQuery(id+"F0.wireOp",EDGE,"E13.33.0.11"),sQuery(id+"F0.wireOp",EDGE,"E13.33.0.12"),sQuery(id+"F0.wireOp",EDGE,"E13.33.0.13"),sQuery(id+"F0.wireOp",EDGE,"E13.33.0.14"),sQuery(id+"F0.wireOp",EDGE,"E13.34.0.0"),sQuery(id+"F0.wireOp",EDGE,"E13.34.0.3"),sQuery(id+"F0.wireOp",EDGE,"E13.34.0.8"),sQuery(id+"F0.wireOp",EDGE,"E13.34.0.9"),sQuery(id+"F0.wireOp",EDGE,"E13.34.0.11"),sQuery(id+"F0.wireOp",EDGE,"E13.34.0.12"),sQuery(id+"F0.wireOp",EDGE,"E13.34.0.13"),sQuery(id+"F0.wireOp",EDGE,"E13.34.0.14"),sQuery(id+"F0.wireOp",EDGE,"E13.35.0.0"),sQuery(id+"F0.wireOp",EDGE,"E13.35.0.3"),sQuery(id+"F0.wireOp",EDGE,"E13.35.0.8"),sQuery(id+"F0.wireOp",EDGE,"E13.35.0.9"),sQuery(id+"F0.wireOp",EDGE,"E13.35.0.11"),sQuery(id+"F0.wireOp",EDGE,"E13.35.0.12"),sQuery(id+"F0.wireOp",EDGE,"E13.35.0.13"),sQuery(id+"F0.wireOp",EDGE,"E13.35.0.14"),sQuery(id+"F0.wireOp",EDGE,"E13.36.0.0"),sQuery(id+"F0.wireOp",EDGE,"E13.36.0.3"),sQuery(id+"F0.wireOp",EDGE,"E13.36.0.8"),sQuery(id+"F0.wireOp",EDGE,"E13.36.0.9"),sQuery(id+"F0.wireOp",EDGE,"E13.36.0.11"),sQuery(id+"F0.wireOp",EDGE,"E13.36.0.12"),sQuery(id+"F0.wireOp",EDGE,"E13.36.0.13"),sQuery(id+"F0.wireOp",EDGE,"E13.36.0.14"),sQuery(id+"F0.wireOp",EDGE,"E13.37.0.0"),sQuery(id+"F0.wireOp",EDGE,"E13.37.0.3"),sQuery(id+"F0.wireOp",EDGE,"E13.37.0.8"),sQuery(id+"F0.wireOp",EDGE,"E13.37.0.9"),sQuery(id+"F0.wireOp",EDGE,"E13.37.0.11"),sQuery(id+"F0.wireOp",EDGE,"E13.37.0.12"),sQuery(id+"F0.wireOp",EDGE,"E13.37.0.13"),sQuery(id+"F0.wireOp",EDGE,"E13.37.0.14"),sQuery(id+"F0.wireOp",EDGE,"E13.38.0.0"),sQuery(id+"F0.wireOp",EDGE,"E13.38.0.3"),sQuery(id+"F0.wireOp",EDGE,"E13.38.0.8"),sQuery(id+"F0.wireOp",EDGE,"E13.38.0.9"),sQuery(id+"F0.wireOp",EDGE,"E13.38.0.11"),sQuery(id+"F0.wireOp",EDGE,"E13.38.0.12"),sQuery(id+"F0.wireOp",EDGE,"E13.38.0.13"),sQuery(id+"F0.wireOp",EDGE,"E13.38.0.14"),sQuery(id+"F0.wireOp",EDGE,"E13.39.0.0"),sQuery(id+"F0.wireOp",EDGE,"E13.39.0.2"),sQuery(id+"F0.wireOp",EDGE,"E13.39.0.3"),sQuery(id+"F0.wireOp",EDGE,"E13.39.0.8"),sQuery(id+"F0.wireOp",EDGE,"E13.39.0.9"),sQuery(id+"F0.wireOp",EDGE,"E13.39.0.11"),sQuery(id+"F0.wireOp",EDGE,"E13.39.0.12"),sQuery(id+"F0.wireOp",EDGE,"E13.39.0.13"),sQuery(id+"F0.wireOp",EDGE,"E13.39.0.14")])],"isStart":true});
            var sketch = newSketch(context, id + "F4", { "sketchPlane" : qUnion([Q0])});
            skLineSegment(sketch, "E16.bottom", {"start": v(47.1, -3) * mm, "end": v(-0.3, -3) * mm});
            skLineSegment(sketch, "E16.top", {"start": v(47.1, -2) * mm, "end": v(-0.3, -2) * mm});
            skLineSegment(sketch, "E16.left", {"start": v(47.1, -2) * mm, "end": v(47.1, -3) * mm});
            skLineSegment(sketch, "E16.right", {"start": v(-0.3, -2) * mm, "end": v(-0.3, -3) * mm});
            skSolve(sketch);
        }
        {
            var Q0;
            Q0=makeQuery(id+"F4.imprint","IMPRINT",FACE,{"disambiguationData":[TD([[makeQuery(id+"F4.imprint","IMPRINT",EDGE,{"derivedFrom":sQuery(id+"F4.wireOp",EDGE,"E16.bottom")}),-1.0]])]});
            extrude(context, id + "F5", {"entities" : qUnion([Q0]), "operationType" : NewBodyOperationType.ADD, "depth" : 10 * mm});
        }
    });
